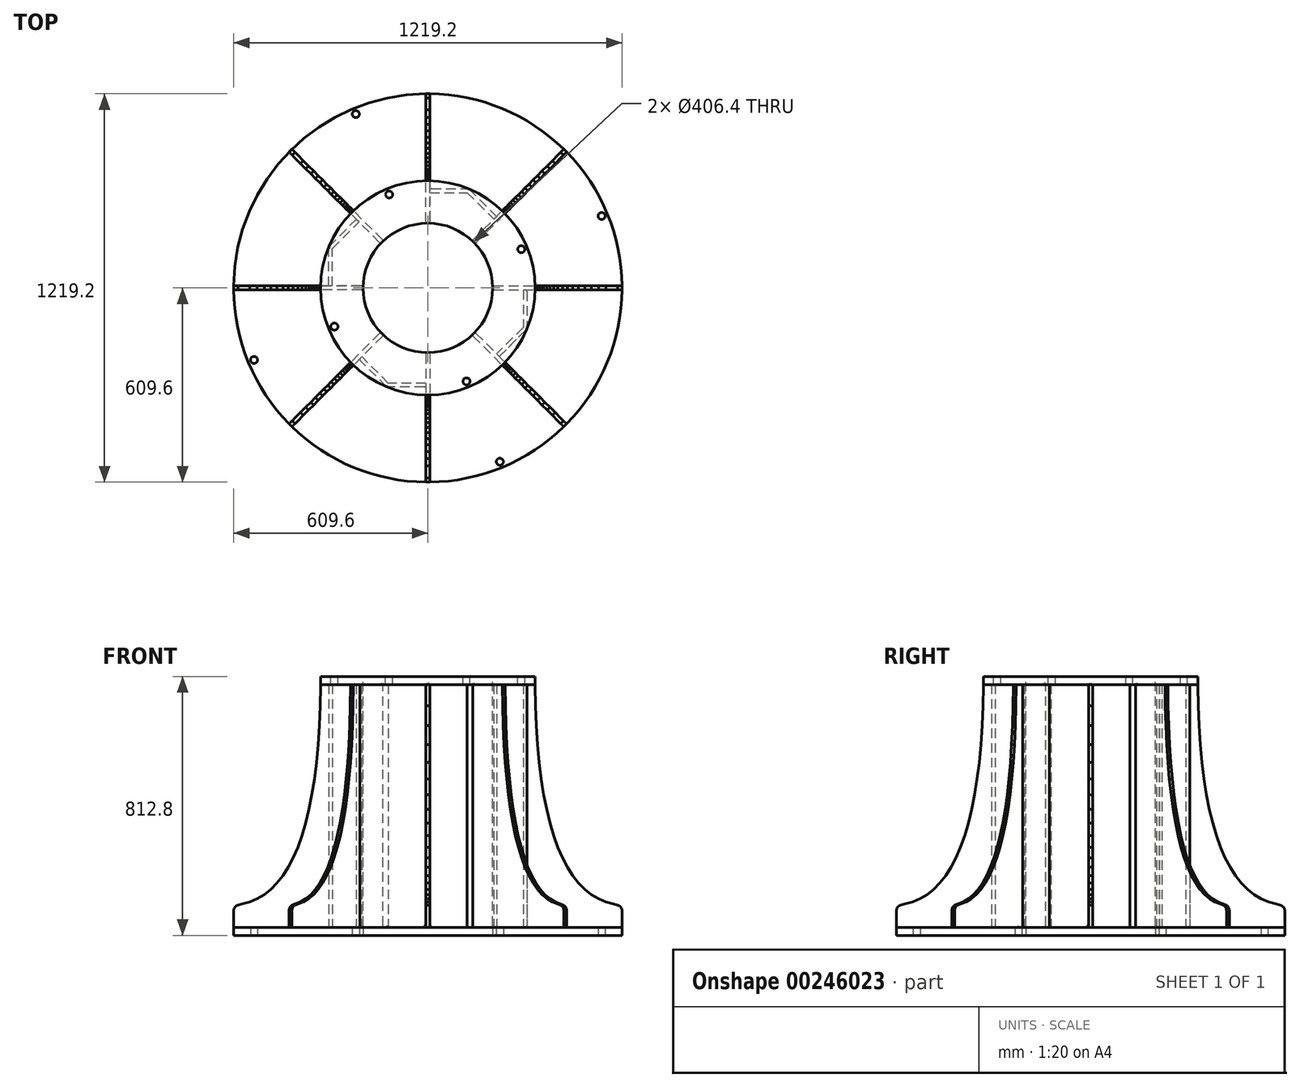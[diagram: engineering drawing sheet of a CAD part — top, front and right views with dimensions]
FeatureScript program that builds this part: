
annotation { "Feature Type Name" : "Feature", "Feature Type Description" : "" }
export const myFeature = defineFeature(function(context is Context, id is Id, definition is map)
    precondition{}
    {
        {
            var Q0;
            Q0=qCreatedBy(makeId("Top.planeOp"),FACE);
            var sketch = newSketch(context, id + "F0", { "sketchPlane" : qUnion([Q0])});
            skCircle(sketch, "E0", {"center": v(0, 0) * mm, "radius": 203.2 * mm});
            skCircle(sketch, "E1", {"center": v(0, 0) * mm, "radius": 195.26 * mm});
            skSolve(sketch);
        }
        {
            var Q0;
            Q0 = qSketchRegion(id + "F0", true);
            extrude(context, id + "F1", {"entities" : qUnion([Q0]), "depth" : 812.8 * mm});
        }
        {
            var Q0;
            Q0=makeQuery(id+"F1.opExtrude","CAP_FACE",FACE,{"disambiguationData":[OSD([sQuery(id+"F0.wireOp",EDGE,"E0"),sQuery(id+"F0.wireOp",EDGE,"E1")])],"isStart":false});
            var sketch = newSketch(context, id + "F2", { "sketchPlane" : qUnion([Q0])});
            skCircle(sketch, "E2", {"center": v(0, 0) * mm, "radius": 203.2 * mm});
            skCircle(sketch, "E3", {"center": v(0, 0) * mm, "radius": 336.55 * mm});
            skCircle(sketch, "E4", {"center": v(0, 0) * mm, "radius": 317.5 * mm, "construction": true});
            skLineSegment(sketch, "E5", {"start": v(0, 0) * mm, "end": v(500.04, 0) * mm, "construction": true});
            skLineSegment(sketch, "E6", {"start": v(0, 0) * mm, "end": v(466.48, 193.22) * mm, "construction": true});
            skCircle(sketch, "E7", {"center": v(293.33, 121.5) * mm, "radius": 11.1 * mm});
            skCircle(sketch, "E8.1.0", {"center": v(-121.5, 293.33) * mm, "radius": 11.1 * mm});
            skCircle(sketch, "E8.2.0", {"center": v(-293.33, -121.5) * mm, "radius": 11.1 * mm});
            skCircle(sketch, "E8.3.0", {"center": v(121.5, -293.33) * mm, "radius": 11.1 * mm});
            skSolve(sketch);
        }
        {
            var Q0;
            Q0 = qSketchRegion(id + "F2", true);
            extrude(context, id + "F3", {"entities" : qUnion([Q0]), "oppositeDirection" : true, "depth" : 25.4 * mm});
        }
        {
            var Q0;
            Q0=qCreatedBy(makeId("Top.planeOp"),FACE);
            var sketch = newSketch(context, id + "F4", { "sketchPlane" : qUnion([Q0])});
            skCircle(sketch, "E9", {"center": v(0, 0) * mm, "radius": 609.6 * mm});
            skCircle(sketch, "E10", {"center": v(0, 0) * mm, "radius": 203.2 * mm});
            skLineSegment(sketch, "E11", {"start": v(0, 0) * mm, "end": v(1083.18, 0) * mm, "construction": true});
            skLineSegment(sketch, "E12", {"start": v(0, 0) * mm, "end": v(912.89, 378.13) * mm, "construction": true});
            skCircle(sketch, "E13", {"center": v(0, 0) * mm, "radius": 590.55 * mm, "construction": true});
            skCircle(sketch, "E14", {"center": v(545.6, 226) * mm, "radius": 11.1 * mm});
            skCircle(sketch, "E15.1.0", {"center": v(-226, 545.6) * mm, "radius": 11.1 * mm});
            skCircle(sketch, "E15.2.0", {"center": v(-545.6, -226) * mm, "radius": 11.1 * mm});
            skCircle(sketch, "E15.3.0", {"center": v(226, -545.6) * mm, "radius": 11.1 * mm});
            skSolve(sketch);
        }
        {
            var Q0;
            Q0 = qSketchRegion(id + "F4", true);
            extrude(context, id + "F5", {"entities" : qUnion([Q0]), "depth" : 25.4 * mm});
        }
        {
            var Q0;
            Q0=qCreatedBy(makeId("Front.planeOp"),FACE);
            var sketch = newSketch(context, id + "F6", { "sketchPlane" : qUnion([Q0])});
            skLineSegment(sketch, "E16", {"start": v(0, 25.4) * mm, "end": v(726.2, 25.4) * mm, "construction": true});
            skLineSegment(sketch, "E17", {"start": v(0, 0) * mm, "end": v(737.94, 0) * mm, "construction": true});
            skLineSegment(sketch, "E18", {"start": v(0, 787.4) * mm, "end": v(419.86, 787.4) * mm, "construction": true});
            skLineSegment(sketch, "E19", {"start": v(0, 0) * mm, "end": v(0, 828.8) * mm, "construction": true});
            skLineSegment(sketch, "E20", {"start": v(0, 787.4) * mm, "end": v(336.55, 787.4) * mm});
            skLineSegment(sketch, "E21", {"start": v(336.55, 787.4) * mm, "end": v(337.85, 721.48) * mm});
            skLineSegment(sketch, "E22", {"start": v(337.85, 721.48) * mm, "end": v(340.45, 658.85) * mm});
            skLineSegment(sketch, "E23", {"start": v(340.45, 658.85) * mm, "end": v(344.35, 599.52) * mm});
            skLineSegment(sketch, "E24", {"start": v(344.35, 599.52) * mm, "end": v(349.55, 543.48) * mm});
            skLineSegment(sketch, "E25", {"start": v(349.55, 543.48) * mm, "end": v(356.05, 490.74) * mm});
            skLineSegment(sketch, "E26", {"start": v(356.05, 490.74) * mm, "end": v(363.86, 441.3) * mm});
            skLineSegment(sketch, "E27", {"start": v(363.86, 441.3) * mm, "end": v(372.96, 395.15) * mm});
            skLineSegment(sketch, "E28", {"start": v(372.96, 395.15) * mm, "end": v(383.36, 352.3) * mm});
            skLineSegment(sketch, "E29", {"start": v(383.36, 352.3) * mm, "end": v(395.06, 312.75) * mm});
            skLineSegment(sketch, "E30", {"start": v(395.06, 312.75) * mm, "end": v(408.06, 276.5) * mm});
            skLineSegment(sketch, "E31", {"start": v(408.06, 276.5) * mm, "end": v(422.37, 243.53) * mm});
            skLineSegment(sketch, "E32", {"start": v(422.37, 243.53) * mm, "end": v(437.97, 213.86) * mm});
            skLineSegment(sketch, "E33", {"start": v(437.97, 213.86) * mm, "end": v(454.87, 187.5) * mm});
            skLineSegment(sketch, "E34", {"start": v(454.87, 187.5) * mm, "end": v(473.08, 164.42) * mm});
            skLineSegment(sketch, "E35", {"start": v(473.08, 164.42) * mm, "end": v(492.58, 144.64) * mm});
            skLineSegment(sketch, "E36", {"start": v(492.58, 144.64) * mm, "end": v(513.38, 128.16) * mm});
            skLineSegment(sketch, "E37", {"start": v(513.38, 128.16) * mm, "end": v(535.49, 114.98) * mm});
            skLineSegment(sketch, "E38", {"start": v(535.49, 114.98) * mm, "end": v(558.9, 105.09) * mm});
            skLineSegment(sketch, "E39", {"start": v(558.9, 105.09) * mm, "end": v(583.6, 98.5) * mm});
            skLineSegment(sketch, "E40", {"start": v(583.6, 98.5) * mm, "end": v(595.94, 95.17) * mm});
            skArc(sketch, "E41", {"start": v(595.94, 95.17) * mm, "mid": v(605.83, 87.89) * mm, "end": v(609.6, 76.2) * mm});
            skLineSegment(sketch, "E42", {"start": v(609.6, 76.2) * mm, "end": v(609.6, 25.4) * mm});
            skLineSegment(sketch, "E43", {"start": v(609.6, 25.4) * mm, "end": v(0, 25.4) * mm});
            skLineSegment(sketch, "E44", {"start": v(0, 25.4) * mm, "end": v(0, 787.4) * mm});
            skSolve(sketch);
        }
        {
            var Q0;
            Q0 = qSketchRegion(id + "F6", true);
            extrude(context, id + "F7", {"entities" : qUnion([Q0]), "depth" : 12.7 * mm, "symmetric" : true});
        }
        {
            var Q0;
            Q0=qCreatedBy(makeId("Top.planeOp"),FACE);
            var sketch = newSketch(context, id + "F8", { "sketchPlane" : qUnion([Q0])});
            skCircle(sketch, "E45", {"center": v(0, 0) * mm, "radius": 203.2 * mm});
            skSolve(sketch);
        }
        {
            var Q0;
            Q0=makeQuery(id+"F8.imprint","IMPRINT",FACE,{"disambiguationData":[TD([[makeQuery(id+"F8.imprint","IMPRINT",EDGE,{"derivedFrom":sQuery(id+"F8.wireOp",EDGE,"E45")}),1.0]])]});
            extrude(context, id + "F9", {"entities" : qUnion([Q0]), "operationType" : NewBodyOperationType.REMOVE, "depth" : 812.8 * mm, "offsetDistance" : 25 * mm});
        }
        {
            var Q0;
            Q0=makeQuery(id+"F7.opExtrude","SWEPT_BODY",BODY,{"disambiguationData":[OSD([sQuery(id+"F6.wireOp",EDGE,"E20"),sQuery(id+"F6.wireOp",EDGE,"E21"),sQuery(id+"F6.wireOp",EDGE,"E22"),sQuery(id+"F6.wireOp",EDGE,"E23"),sQuery(id+"F6.wireOp",EDGE,"E24"),sQuery(id+"F6.wireOp",EDGE,"E25"),sQuery(id+"F6.wireOp",EDGE,"E26"),sQuery(id+"F6.wireOp",EDGE,"E27"),sQuery(id+"F6.wireOp",EDGE,"E28"),sQuery(id+"F6.wireOp",EDGE,"E29"),sQuery(id+"F6.wireOp",EDGE,"E30"),sQuery(id+"F6.wireOp",EDGE,"E31"),sQuery(id+"F6.wireOp",EDGE,"E32"),sQuery(id+"F6.wireOp",EDGE,"E33"),sQuery(id+"F6.wireOp",EDGE,"E34"),sQuery(id+"F6.wireOp",EDGE,"E35"),sQuery(id+"F6.wireOp",EDGE,"E36"),sQuery(id+"F6.wireOp",EDGE,"E37"),sQuery(id+"F6.wireOp",EDGE,"E38"),sQuery(id+"F6.wireOp",EDGE,"E39"),sQuery(id+"F6.wireOp",EDGE,"E40"),sQuery(id+"F6.wireOp",EDGE,"E41"),sQuery(id+"F6.wireOp",EDGE,"E42"),sQuery(id+"F6.wireOp",EDGE,"E43"),sQuery(id+"F6.wireOp",EDGE,"E44")])]});
            var Q1;
            Q1=sQuery(id+"F6.wireOp",EDGE,"E19");
            circularPattern(context, id + "F10", {"entities" : qUnion([Q0]), "axis" : qUnion([Q1]), "angle" : 360 * degree, "instanceCount" : 8, "equalSpace" : true});
        }
        {
            var Q0;
            Q0=makeQuery(id+"F5.opExtrude","CAP_FACE",FACE,{"disambiguationData":[OSD([sQuery(id+"F4.wireOp",EDGE,"E9"),sQuery(id+"F4.wireOp",EDGE,"E10"),sQuery(id+"F4.wireOp",EDGE,"E14"),sQuery(id+"F4.wireOp",EDGE,"E15.1.0"),sQuery(id+"F4.wireOp",EDGE,"E15.2.0"),sQuery(id+"F4.wireOp",EDGE,"E15.3.0")])],"isStart":false});
            var sketch = newSketch(context, id + "F11", { "sketchPlane" : qUnion([Q0])});
            skCircle(sketch, "E46", {"center": v(0, 0) * mm, "radius": 323.85 * mm, "construction": true});
            skCircle(sketch, "E47", {"center": v(0, 0) * mm, "radius": 336.55 * mm, "construction": true});
            skLineSegment(sketch, "E48", {"start": v(0, 0) * mm, "end": v(904.77, 0) * mm, "construction": true});
            skLineSegment(sketch, "E49", {"start": v(0, 0) * mm, "end": v(0, 713.88) * mm, "construction": true});
            skLineSegment(sketch, "E50", {"start": v(0, 0) * mm, "end": v(749.37, 310.4) * mm, "construction": true});
            skLineSegment(sketch, "E51.7", {"start": v(128.8, 310.93) * mm, "end": v(215.37, 224.35) * mm});
            skLineSegment(sketch, "E52.7", {"start": v(123.93, 299.2) * mm, "end": v(207.08, 216.06) * mm});
            skLineSegment(sketch, "E53.1.1", {"start": v(0, 0) * mm, "end": v(504.79, 504.79) * mm, "construction": true});
            skLineSegment(sketch, "E54.trimOffspring", {"start": v(207.08, 216.06) * mm, "end": v(215.37, 224.35) * mm});
            skLineSegment(sketch, "E55.trimOffspring", {"start": v(6.35, 299.2) * mm, "end": v(123.93, 299.2) * mm});
            skLineSegment(sketch, "E56.trimOffspring", {"start": v(6.35, 310.93) * mm, "end": v(128.8, 310.93) * mm});
            skLineSegment(sketch, "E57.trimOffspring", {"start": v(6.35, 299.2) * mm, "end": v(6.35, 310.93) * mm});
            skSolve(sketch);
        }
        {
            var Q0;
            Q0=makeQuery(id+"F11.imprint","IMPRINT",FACE,{"disambiguationData":[TD([[makeQuery(id+"F11.imprint","IMPRINT",EDGE,{"derivedFrom":sQuery(id+"F11.wireOp",EDGE,"E51.7")}),-1.0]])]});
            extrude(context, id + "F12", {"entities" : qUnion([Q0]), "depth" : 762 * mm});
        }
        {
            var Q0;
            Q0=makeQuery(id+"F12.opExtrude","SWEPT_BODY",BODY,{"disambiguationData":[OSD([sQuery(id+"F11.wireOp",EDGE,"E51.7"),sQuery(id+"F11.wireOp",EDGE,"E52.7"),sQuery(id+"F11.wireOp",EDGE,"E54.trimOffspring"),sQuery(id+"F11.wireOp",EDGE,"E55.trimOffspring"),sQuery(id+"F11.wireOp",EDGE,"E56.trimOffspring"),sQuery(id+"F11.wireOp",EDGE,"E57.trimOffspring")])]});
            var Q1;
            Q1=sQuery(id+"F6.wireOp",EDGE,"E44");
            circularPattern(context, id + "F13", {"entities" : qUnion([Q0]), "axis" : qUnion([Q1]), "angle" : 360 * degree, "instanceCount" : 4, "equalSpace" : true});
        }
        {
            var Q0;
            Q0=makeQuery(id+"F3.opExtrude","SWEPT_BODY",BODY,{"disambiguationData":[OSD([sQuery(id+"F2.wireOp",EDGE,"E2"),sQuery(id+"F2.wireOp",EDGE,"E3"),sQuery(id+"F2.wireOp",EDGE,"E7"),sQuery(id+"F2.wireOp",EDGE,"E8.1.0"),sQuery(id+"F2.wireOp",EDGE,"E8.2.0"),sQuery(id+"F2.wireOp",EDGE,"E8.3.0")])]});
            var Q1;
            Q1=makeQuery(id+"F10.opPattern","COPY",BODY,{"derivedFrom":makeQuery(id+"F7.opExtrude","SWEPT_BODY",BODY,{"disambiguationData":[OSD([sQuery(id+"F6.wireOp",EDGE,"E20"),sQuery(id+"F6.wireOp",EDGE,"E21"),sQuery(id+"F6.wireOp",EDGE,"E22"),sQuery(id+"F6.wireOp",EDGE,"E23"),sQuery(id+"F6.wireOp",EDGE,"E24"),sQuery(id+"F6.wireOp",EDGE,"E25"),sQuery(id+"F6.wireOp",EDGE,"E26"),sQuery(id+"F6.wireOp",EDGE,"E27"),sQuery(id+"F6.wireOp",EDGE,"E28"),sQuery(id+"F6.wireOp",EDGE,"E29"),sQuery(id+"F6.wireOp",EDGE,"E30"),sQuery(id+"F6.wireOp",EDGE,"E31"),sQuery(id+"F6.wireOp",EDGE,"E32"),sQuery(id+"F6.wireOp",EDGE,"E33"),sQuery(id+"F6.wireOp",EDGE,"E34"),sQuery(id+"F6.wireOp",EDGE,"E35"),sQuery(id+"F6.wireOp",EDGE,"E36"),sQuery(id+"F6.wireOp",EDGE,"E37"),sQuery(id+"F6.wireOp",EDGE,"E38"),sQuery(id+"F6.wireOp",EDGE,"E39"),sQuery(id+"F6.wireOp",EDGE,"E40"),sQuery(id+"F6.wireOp",EDGE,"E41"),sQuery(id+"F6.wireOp",EDGE,"E42"),sQuery(id+"F6.wireOp",EDGE,"E43"),sQuery(id+"F6.wireOp",EDGE,"E44")])]}),"instanceName":"7"});
            var Q2;
            Q2=makeQuery(id+"F7.opExtrude","SWEPT_BODY",BODY,{"disambiguationData":[OSD([sQuery(id+"F6.wireOp",EDGE,"E20"),sQuery(id+"F6.wireOp",EDGE,"E21"),sQuery(id+"F6.wireOp",EDGE,"E22"),sQuery(id+"F6.wireOp",EDGE,"E23"),sQuery(id+"F6.wireOp",EDGE,"E24"),sQuery(id+"F6.wireOp",EDGE,"E25"),sQuery(id+"F6.wireOp",EDGE,"E26"),sQuery(id+"F6.wireOp",EDGE,"E27"),sQuery(id+"F6.wireOp",EDGE,"E28"),sQuery(id+"F6.wireOp",EDGE,"E29"),sQuery(id+"F6.wireOp",EDGE,"E30"),sQuery(id+"F6.wireOp",EDGE,"E31"),sQuery(id+"F6.wireOp",EDGE,"E32"),sQuery(id+"F6.wireOp",EDGE,"E33"),sQuery(id+"F6.wireOp",EDGE,"E34"),sQuery(id+"F6.wireOp",EDGE,"E35"),sQuery(id+"F6.wireOp",EDGE,"E36"),sQuery(id+"F6.wireOp",EDGE,"E37"),sQuery(id+"F6.wireOp",EDGE,"E38"),sQuery(id+"F6.wireOp",EDGE,"E39"),sQuery(id+"F6.wireOp",EDGE,"E40"),sQuery(id+"F6.wireOp",EDGE,"E41"),sQuery(id+"F6.wireOp",EDGE,"E42"),sQuery(id+"F6.wireOp",EDGE,"E43"),sQuery(id+"F6.wireOp",EDGE,"E44")])]});
            var Q3;
            Q3=makeQuery(id+"F10.opPattern","COPY",BODY,{"derivedFrom":makeQuery(id+"F7.opExtrude","SWEPT_BODY",BODY,{"disambiguationData":[OSD([sQuery(id+"F6.wireOp",EDGE,"E20"),sQuery(id+"F6.wireOp",EDGE,"E21"),sQuery(id+"F6.wireOp",EDGE,"E22"),sQuery(id+"F6.wireOp",EDGE,"E23"),sQuery(id+"F6.wireOp",EDGE,"E24"),sQuery(id+"F6.wireOp",EDGE,"E25"),sQuery(id+"F6.wireOp",EDGE,"E26"),sQuery(id+"F6.wireOp",EDGE,"E27"),sQuery(id+"F6.wireOp",EDGE,"E28"),sQuery(id+"F6.wireOp",EDGE,"E29"),sQuery(id+"F6.wireOp",EDGE,"E30"),sQuery(id+"F6.wireOp",EDGE,"E31"),sQuery(id+"F6.wireOp",EDGE,"E32"),sQuery(id+"F6.wireOp",EDGE,"E33"),sQuery(id+"F6.wireOp",EDGE,"E34"),sQuery(id+"F6.wireOp",EDGE,"E35"),sQuery(id+"F6.wireOp",EDGE,"E36"),sQuery(id+"F6.wireOp",EDGE,"E37"),sQuery(id+"F6.wireOp",EDGE,"E38"),sQuery(id+"F6.wireOp",EDGE,"E39"),sQuery(id+"F6.wireOp",EDGE,"E40"),sQuery(id+"F6.wireOp",EDGE,"E41"),sQuery(id+"F6.wireOp",EDGE,"E42"),sQuery(id+"F6.wireOp",EDGE,"E43"),sQuery(id+"F6.wireOp",EDGE,"E44")])]}),"instanceName":"1"});
            var Q4;
            Q4=makeQuery(id+"F10.opPattern","COPY",BODY,{"derivedFrom":makeQuery(id+"F7.opExtrude","SWEPT_BODY",BODY,{"disambiguationData":[OSD([sQuery(id+"F6.wireOp",EDGE,"E20"),sQuery(id+"F6.wireOp",EDGE,"E21"),sQuery(id+"F6.wireOp",EDGE,"E22"),sQuery(id+"F6.wireOp",EDGE,"E23"),sQuery(id+"F6.wireOp",EDGE,"E24"),sQuery(id+"F6.wireOp",EDGE,"E25"),sQuery(id+"F6.wireOp",EDGE,"E26"),sQuery(id+"F6.wireOp",EDGE,"E27"),sQuery(id+"F6.wireOp",EDGE,"E28"),sQuery(id+"F6.wireOp",EDGE,"E29"),sQuery(id+"F6.wireOp",EDGE,"E30"),sQuery(id+"F6.wireOp",EDGE,"E31"),sQuery(id+"F6.wireOp",EDGE,"E32"),sQuery(id+"F6.wireOp",EDGE,"E33"),sQuery(id+"F6.wireOp",EDGE,"E34"),sQuery(id+"F6.wireOp",EDGE,"E35"),sQuery(id+"F6.wireOp",EDGE,"E36"),sQuery(id+"F6.wireOp",EDGE,"E37"),sQuery(id+"F6.wireOp",EDGE,"E38"),sQuery(id+"F6.wireOp",EDGE,"E39"),sQuery(id+"F6.wireOp",EDGE,"E40"),sQuery(id+"F6.wireOp",EDGE,"E41"),sQuery(id+"F6.wireOp",EDGE,"E42"),sQuery(id+"F6.wireOp",EDGE,"E43"),sQuery(id+"F6.wireOp",EDGE,"E44")])]}),"instanceName":"2"});
            var Q5;
            Q5=makeQuery(id+"F10.opPattern","COPY",BODY,{"derivedFrom":makeQuery(id+"F7.opExtrude","SWEPT_BODY",BODY,{"disambiguationData":[OSD([sQuery(id+"F6.wireOp",EDGE,"E20"),sQuery(id+"F6.wireOp",EDGE,"E21"),sQuery(id+"F6.wireOp",EDGE,"E22"),sQuery(id+"F6.wireOp",EDGE,"E23"),sQuery(id+"F6.wireOp",EDGE,"E24"),sQuery(id+"F6.wireOp",EDGE,"E25"),sQuery(id+"F6.wireOp",EDGE,"E26"),sQuery(id+"F6.wireOp",EDGE,"E27"),sQuery(id+"F6.wireOp",EDGE,"E28"),sQuery(id+"F6.wireOp",EDGE,"E29"),sQuery(id+"F6.wireOp",EDGE,"E30"),sQuery(id+"F6.wireOp",EDGE,"E31"),sQuery(id+"F6.wireOp",EDGE,"E32"),sQuery(id+"F6.wireOp",EDGE,"E33"),sQuery(id+"F6.wireOp",EDGE,"E34"),sQuery(id+"F6.wireOp",EDGE,"E35"),sQuery(id+"F6.wireOp",EDGE,"E36"),sQuery(id+"F6.wireOp",EDGE,"E37"),sQuery(id+"F6.wireOp",EDGE,"E38"),sQuery(id+"F6.wireOp",EDGE,"E39"),sQuery(id+"F6.wireOp",EDGE,"E40"),sQuery(id+"F6.wireOp",EDGE,"E41"),sQuery(id+"F6.wireOp",EDGE,"E42"),sQuery(id+"F6.wireOp",EDGE,"E43"),sQuery(id+"F6.wireOp",EDGE,"E44")])]}),"instanceName":"3"});
            var Q6;
            Q6=makeQuery(id+"F10.opPattern","COPY",BODY,{"derivedFrom":makeQuery(id+"F7.opExtrude","SWEPT_BODY",BODY,{"disambiguationData":[OSD([sQuery(id+"F6.wireOp",EDGE,"E20"),sQuery(id+"F6.wireOp",EDGE,"E21"),sQuery(id+"F6.wireOp",EDGE,"E22"),sQuery(id+"F6.wireOp",EDGE,"E23"),sQuery(id+"F6.wireOp",EDGE,"E24"),sQuery(id+"F6.wireOp",EDGE,"E25"),sQuery(id+"F6.wireOp",EDGE,"E26"),sQuery(id+"F6.wireOp",EDGE,"E27"),sQuery(id+"F6.wireOp",EDGE,"E28"),sQuery(id+"F6.wireOp",EDGE,"E29"),sQuery(id+"F6.wireOp",EDGE,"E30"),sQuery(id+"F6.wireOp",EDGE,"E31"),sQuery(id+"F6.wireOp",EDGE,"E32"),sQuery(id+"F6.wireOp",EDGE,"E33"),sQuery(id+"F6.wireOp",EDGE,"E34"),sQuery(id+"F6.wireOp",EDGE,"E35"),sQuery(id+"F6.wireOp",EDGE,"E36"),sQuery(id+"F6.wireOp",EDGE,"E37"),sQuery(id+"F6.wireOp",EDGE,"E38"),sQuery(id+"F6.wireOp",EDGE,"E39"),sQuery(id+"F6.wireOp",EDGE,"E40"),sQuery(id+"F6.wireOp",EDGE,"E41"),sQuery(id+"F6.wireOp",EDGE,"E42"),sQuery(id+"F6.wireOp",EDGE,"E43"),sQuery(id+"F6.wireOp",EDGE,"E44")])]}),"instanceName":"4"});
            var Q7;
            Q7=makeQuery(id+"F10.opPattern","COPY",BODY,{"derivedFrom":makeQuery(id+"F7.opExtrude","SWEPT_BODY",BODY,{"disambiguationData":[OSD([sQuery(id+"F6.wireOp",EDGE,"E20"),sQuery(id+"F6.wireOp",EDGE,"E21"),sQuery(id+"F6.wireOp",EDGE,"E22"),sQuery(id+"F6.wireOp",EDGE,"E23"),sQuery(id+"F6.wireOp",EDGE,"E24"),sQuery(id+"F6.wireOp",EDGE,"E25"),sQuery(id+"F6.wireOp",EDGE,"E26"),sQuery(id+"F6.wireOp",EDGE,"E27"),sQuery(id+"F6.wireOp",EDGE,"E28"),sQuery(id+"F6.wireOp",EDGE,"E29"),sQuery(id+"F6.wireOp",EDGE,"E30"),sQuery(id+"F6.wireOp",EDGE,"E31"),sQuery(id+"F6.wireOp",EDGE,"E32"),sQuery(id+"F6.wireOp",EDGE,"E33"),sQuery(id+"F6.wireOp",EDGE,"E34"),sQuery(id+"F6.wireOp",EDGE,"E35"),sQuery(id+"F6.wireOp",EDGE,"E36"),sQuery(id+"F6.wireOp",EDGE,"E37"),sQuery(id+"F6.wireOp",EDGE,"E38"),sQuery(id+"F6.wireOp",EDGE,"E39"),sQuery(id+"F6.wireOp",EDGE,"E40"),sQuery(id+"F6.wireOp",EDGE,"E41"),sQuery(id+"F6.wireOp",EDGE,"E42"),sQuery(id+"F6.wireOp",EDGE,"E43"),sQuery(id+"F6.wireOp",EDGE,"E44")])]}),"instanceName":"5"});
            var Q8;
            Q8=makeQuery(id+"F10.opPattern","COPY",BODY,{"derivedFrom":makeQuery(id+"F7.opExtrude","SWEPT_BODY",BODY,{"disambiguationData":[OSD([sQuery(id+"F6.wireOp",EDGE,"E20"),sQuery(id+"F6.wireOp",EDGE,"E21"),sQuery(id+"F6.wireOp",EDGE,"E22"),sQuery(id+"F6.wireOp",EDGE,"E23"),sQuery(id+"F6.wireOp",EDGE,"E24"),sQuery(id+"F6.wireOp",EDGE,"E25"),sQuery(id+"F6.wireOp",EDGE,"E26"),sQuery(id+"F6.wireOp",EDGE,"E27"),sQuery(id+"F6.wireOp",EDGE,"E28"),sQuery(id+"F6.wireOp",EDGE,"E29"),sQuery(id+"F6.wireOp",EDGE,"E30"),sQuery(id+"F6.wireOp",EDGE,"E31"),sQuery(id+"F6.wireOp",EDGE,"E32"),sQuery(id+"F6.wireOp",EDGE,"E33"),sQuery(id+"F6.wireOp",EDGE,"E34"),sQuery(id+"F6.wireOp",EDGE,"E35"),sQuery(id+"F6.wireOp",EDGE,"E36"),sQuery(id+"F6.wireOp",EDGE,"E37"),sQuery(id+"F6.wireOp",EDGE,"E38"),sQuery(id+"F6.wireOp",EDGE,"E39"),sQuery(id+"F6.wireOp",EDGE,"E40"),sQuery(id+"F6.wireOp",EDGE,"E41"),sQuery(id+"F6.wireOp",EDGE,"E42"),sQuery(id+"F6.wireOp",EDGE,"E43"),sQuery(id+"F6.wireOp",EDGE,"E44")])]}),"instanceName":"6"});
            booleanBodies(context, id + "F14", {"operationType" : BooleanOperationType.UNION, "tools" : qUnion([Q0, Q1, Q2, Q3, Q4, Q5, Q6, Q7, Q8])});
        }
        {
            var Q0;
            {var subQ0=sQuery(id+"F6.wireOp",EDGE,"E43");Q0=makeQuery(id+"F14.opBoolean","SPLIT",EDGE,{"disambiguationData":[TD([makeQuery(id+"F1.opExtrude","SWEPT_FACE",FACE,{"disambiguationData":[OSD([sQuery(id+"F0.wireOp",EDGE,"E0")])]})])],"derivedFrom":makeQuery(id+"F10.opPattern","COPY",EDGE,{"derivedFrom":makeQuery(id+"F7.opExtrude","CAP_EDGE",EDGE,{"disambiguationData":[OSD([subQ0])],"isStart":false}),"instanceName":"3"})});}
            var Q1;
            {var subQ0=sQuery(id+"F4.wireOp",EDGE,"E10");var subQ1=sQuery(id+"F6.wireOp",EDGE,"E44");var subQ2=sQuery(id+"F6.wireOp",EDGE,"E43");var subQ3=sQuery(id+"F6.wireOp",EDGE,"E42");var subQ4=sQuery(id+"F6.wireOp",EDGE,"E41");var subQ5=sQuery(id+"F6.wireOp",EDGE,"E40");var subQ6=sQuery(id+"F6.wireOp",EDGE,"E39");var subQ7=sQuery(id+"F6.wireOp",EDGE,"E38");var subQ8=sQuery(id+"F6.wireOp",EDGE,"E37");var subQ9=sQuery(id+"F6.wireOp",EDGE,"E36");var subQ10=sQuery(id+"F6.wireOp",EDGE,"E35");var subQ11=sQuery(id+"F6.wireOp",EDGE,"E34");var subQ12=sQuery(id+"F6.wireOp",EDGE,"E33");var subQ13=sQuery(id+"F6.wireOp",EDGE,"E32");var subQ14=sQuery(id+"F6.wireOp",EDGE,"E31");var subQ15=sQuery(id+"F6.wireOp",EDGE,"E30");var subQ16=sQuery(id+"F6.wireOp",EDGE,"E29");var subQ17=sQuery(id+"F6.wireOp",EDGE,"E28");var subQ18=sQuery(id+"F6.wireOp",EDGE,"E27");var subQ19=sQuery(id+"F6.wireOp",EDGE,"E26");var subQ20=sQuery(id+"F6.wireOp",EDGE,"E25");var subQ21=sQuery(id+"F6.wireOp",EDGE,"E24");var subQ22=sQuery(id+"F6.wireOp",EDGE,"E23");var subQ23=sQuery(id+"F6.wireOp",EDGE,"E22");var subQ24=sQuery(id+"F6.wireOp",EDGE,"E21");var subQ25=sQuery(id+"F6.wireOp",EDGE,"E20");Q1=makeQuery(id+"F14.opBoolean","SPLIT",EDGE,{"disambiguationData":[TD([makeQuery(id+"F10.opPattern","COPY",FACE,{"derivedFrom":makeQuery(id+"F7.opExtrude","CAP_FACE",FACE,{"disambiguationData":[OSD([subQ25,subQ24,subQ23,subQ22,subQ21,subQ20,subQ19,subQ18,subQ17,subQ16,subQ15,subQ14,subQ13,subQ12,subQ11,subQ10,subQ9,subQ8,subQ7,subQ6,subQ5,subQ4,subQ3,subQ2,subQ1])],"isStart":true}),"instanceName":"2"})])],"derivedFrom":makeQuery(id+"F5.opExtrude","CAP_EDGE",EDGE,{"disambiguationData":[OSD([subQ0])],"isStart":false})});}
            var Q2;
            {var subQ0=sQuery(id+"F6.wireOp",EDGE,"E43");Q2=makeQuery(id+"F14.opBoolean","SPLIT",EDGE,{"disambiguationData":[TD([makeQuery(id+"F1.opExtrude","SWEPT_FACE",FACE,{"disambiguationData":[OSD([sQuery(id+"F0.wireOp",EDGE,"E0")])]})])],"derivedFrom":makeQuery(id+"F10.opPattern","COPY",EDGE,{"derivedFrom":makeQuery(id+"F7.opExtrude","CAP_EDGE",EDGE,{"disambiguationData":[OSD([subQ0])],"isStart":true}),"instanceName":"2"})});}
            var Q3;
            {var subQ0=sQuery(id+"F6.wireOp",EDGE,"E43");Q3=makeQuery(id+"F14.opBoolean","SPLIT",EDGE,{"disambiguationData":[TD([makeQuery(id+"F1.opExtrude","SWEPT_FACE",FACE,{"disambiguationData":[OSD([sQuery(id+"F0.wireOp",EDGE,"E0")])]})])],"derivedFrom":makeQuery(id+"F10.opPattern","COPY",EDGE,{"derivedFrom":makeQuery(id+"F7.opExtrude","CAP_EDGE",EDGE,{"disambiguationData":[OSD([subQ0])],"isStart":false}),"instanceName":"2"})});}
            var Q4;
            {var subQ0=sQuery(id+"F4.wireOp",EDGE,"E10");var subQ1=sQuery(id+"F6.wireOp",EDGE,"E44");var subQ2=sQuery(id+"F6.wireOp",EDGE,"E43");var subQ3=sQuery(id+"F6.wireOp",EDGE,"E42");var subQ4=sQuery(id+"F6.wireOp",EDGE,"E41");var subQ5=sQuery(id+"F6.wireOp",EDGE,"E40");var subQ6=sQuery(id+"F6.wireOp",EDGE,"E39");var subQ7=sQuery(id+"F6.wireOp",EDGE,"E38");var subQ8=sQuery(id+"F6.wireOp",EDGE,"E37");var subQ9=sQuery(id+"F6.wireOp",EDGE,"E36");var subQ10=sQuery(id+"F6.wireOp",EDGE,"E35");var subQ11=sQuery(id+"F6.wireOp",EDGE,"E34");var subQ12=sQuery(id+"F6.wireOp",EDGE,"E33");var subQ13=sQuery(id+"F6.wireOp",EDGE,"E32");var subQ14=sQuery(id+"F6.wireOp",EDGE,"E31");var subQ15=sQuery(id+"F6.wireOp",EDGE,"E30");var subQ16=sQuery(id+"F6.wireOp",EDGE,"E29");var subQ17=sQuery(id+"F6.wireOp",EDGE,"E28");var subQ18=sQuery(id+"F6.wireOp",EDGE,"E27");var subQ19=sQuery(id+"F6.wireOp",EDGE,"E26");var subQ20=sQuery(id+"F6.wireOp",EDGE,"E25");var subQ21=sQuery(id+"F6.wireOp",EDGE,"E24");var subQ22=sQuery(id+"F6.wireOp",EDGE,"E23");var subQ23=sQuery(id+"F6.wireOp",EDGE,"E22");var subQ24=sQuery(id+"F6.wireOp",EDGE,"E21");var subQ25=sQuery(id+"F6.wireOp",EDGE,"E20");Q4=makeQuery(id+"F14.opBoolean","SPLIT",EDGE,{"disambiguationData":[TD([makeQuery(id+"F10.opPattern","COPY",FACE,{"derivedFrom":makeQuery(id+"F7.opExtrude","CAP_FACE",FACE,{"disambiguationData":[OSD([subQ25,subQ24,subQ23,subQ22,subQ21,subQ20,subQ19,subQ18,subQ17,subQ16,subQ15,subQ14,subQ13,subQ12,subQ11,subQ10,subQ9,subQ8,subQ7,subQ6,subQ5,subQ4,subQ3,subQ2,subQ1])],"isStart":true}),"instanceName":"1"})])],"derivedFrom":makeQuery(id+"F5.opExtrude","CAP_EDGE",EDGE,{"disambiguationData":[OSD([subQ0])],"isStart":false})});}
            var Q5;
            {var subQ0=sQuery(id+"F6.wireOp",EDGE,"E43");Q5=makeQuery(id+"F14.opBoolean","SPLIT",EDGE,{"disambiguationData":[TD([makeQuery(id+"F1.opExtrude","SWEPT_FACE",FACE,{"disambiguationData":[OSD([sQuery(id+"F0.wireOp",EDGE,"E0")])]})])],"derivedFrom":makeQuery(id+"F10.opPattern","COPY",EDGE,{"derivedFrom":makeQuery(id+"F7.opExtrude","CAP_EDGE",EDGE,{"disambiguationData":[OSD([subQ0])],"isStart":true}),"instanceName":"1"})});}
            var Q6;
            {var subQ0=sQuery(id+"F6.wireOp",EDGE,"E43");Q6=makeQuery(id+"F14.opBoolean","SPLIT",EDGE,{"disambiguationData":[TD([makeQuery(id+"F1.opExtrude","SWEPT_FACE",FACE,{"disambiguationData":[OSD([sQuery(id+"F0.wireOp",EDGE,"E0")])]})])],"derivedFrom":makeQuery(id+"F10.opPattern","COPY",EDGE,{"derivedFrom":makeQuery(id+"F7.opExtrude","CAP_EDGE",EDGE,{"disambiguationData":[OSD([subQ0])],"isStart":false}),"instanceName":"1"})});}
            var Q7;
            {var subQ0=sQuery(id+"F4.wireOp",EDGE,"E10");var subQ1=sQuery(id+"F6.wireOp",EDGE,"E44");var subQ2=sQuery(id+"F6.wireOp",EDGE,"E43");var subQ3=sQuery(id+"F6.wireOp",EDGE,"E42");var subQ4=sQuery(id+"F6.wireOp",EDGE,"E41");var subQ5=sQuery(id+"F6.wireOp",EDGE,"E40");var subQ6=sQuery(id+"F6.wireOp",EDGE,"E39");var subQ7=sQuery(id+"F6.wireOp",EDGE,"E38");var subQ8=sQuery(id+"F6.wireOp",EDGE,"E37");var subQ9=sQuery(id+"F6.wireOp",EDGE,"E36");var subQ10=sQuery(id+"F6.wireOp",EDGE,"E35");var subQ11=sQuery(id+"F6.wireOp",EDGE,"E34");var subQ12=sQuery(id+"F6.wireOp",EDGE,"E33");var subQ13=sQuery(id+"F6.wireOp",EDGE,"E32");var subQ14=sQuery(id+"F6.wireOp",EDGE,"E31");var subQ15=sQuery(id+"F6.wireOp",EDGE,"E30");var subQ16=sQuery(id+"F6.wireOp",EDGE,"E29");var subQ17=sQuery(id+"F6.wireOp",EDGE,"E28");var subQ18=sQuery(id+"F6.wireOp",EDGE,"E27");var subQ19=sQuery(id+"F6.wireOp",EDGE,"E26");var subQ20=sQuery(id+"F6.wireOp",EDGE,"E25");var subQ21=sQuery(id+"F6.wireOp",EDGE,"E24");var subQ22=sQuery(id+"F6.wireOp",EDGE,"E23");var subQ23=sQuery(id+"F6.wireOp",EDGE,"E22");var subQ24=sQuery(id+"F6.wireOp",EDGE,"E21");var subQ25=sQuery(id+"F6.wireOp",EDGE,"E20");Q7=makeQuery(id+"F14.opBoolean","SPLIT",EDGE,{"disambiguationData":[TD([makeQuery(id+"F7.opExtrude","CAP_FACE",FACE,{"disambiguationData":[OSD([subQ25,subQ24,subQ23,subQ22,subQ21,subQ20,subQ19,subQ18,subQ17,subQ16,subQ15,subQ14,subQ13,subQ12,subQ11,subQ10,subQ9,subQ8,subQ7,subQ6,subQ5,subQ4,subQ3,subQ2,subQ1])],"isStart":true})])],"derivedFrom":makeQuery(id+"F5.opExtrude","CAP_EDGE",EDGE,{"disambiguationData":[OSD([subQ0])],"isStart":false})});}
            var Q8;
            {var subQ0=sQuery(id+"F6.wireOp",EDGE,"E43");Q8=makeQuery(id+"F14.opBoolean","SPLIT",EDGE,{"disambiguationData":[TD([makeQuery(id+"F1.opExtrude","SWEPT_FACE",FACE,{"disambiguationData":[OSD([sQuery(id+"F0.wireOp",EDGE,"E0")])]})])],"derivedFrom":makeQuery(id+"F7.opExtrude","CAP_EDGE",EDGE,{"disambiguationData":[OSD([subQ0])],"isStart":true})});}
            var Q9;
            {var subQ0=sQuery(id+"F6.wireOp",EDGE,"E43");Q9=makeQuery(id+"F14.opBoolean","SPLIT",EDGE,{"disambiguationData":[TD([makeQuery(id+"F1.opExtrude","SWEPT_FACE",FACE,{"disambiguationData":[OSD([sQuery(id+"F0.wireOp",EDGE,"E0")])]})])],"derivedFrom":makeQuery(id+"F7.opExtrude","CAP_EDGE",EDGE,{"disambiguationData":[OSD([subQ0])],"isStart":false})});}
            var Q10;
            {var subQ0=sQuery(id+"F4.wireOp",EDGE,"E10");var subQ1=sQuery(id+"F6.wireOp",EDGE,"E44");var subQ2=sQuery(id+"F6.wireOp",EDGE,"E43");var subQ3=sQuery(id+"F6.wireOp",EDGE,"E42");var subQ4=sQuery(id+"F6.wireOp",EDGE,"E41");var subQ5=sQuery(id+"F6.wireOp",EDGE,"E40");var subQ6=sQuery(id+"F6.wireOp",EDGE,"E39");var subQ7=sQuery(id+"F6.wireOp",EDGE,"E38");var subQ8=sQuery(id+"F6.wireOp",EDGE,"E37");var subQ9=sQuery(id+"F6.wireOp",EDGE,"E36");var subQ10=sQuery(id+"F6.wireOp",EDGE,"E35");var subQ11=sQuery(id+"F6.wireOp",EDGE,"E34");var subQ12=sQuery(id+"F6.wireOp",EDGE,"E33");var subQ13=sQuery(id+"F6.wireOp",EDGE,"E32");var subQ14=sQuery(id+"F6.wireOp",EDGE,"E31");var subQ15=sQuery(id+"F6.wireOp",EDGE,"E30");var subQ16=sQuery(id+"F6.wireOp",EDGE,"E29");var subQ17=sQuery(id+"F6.wireOp",EDGE,"E28");var subQ18=sQuery(id+"F6.wireOp",EDGE,"E27");var subQ19=sQuery(id+"F6.wireOp",EDGE,"E26");var subQ20=sQuery(id+"F6.wireOp",EDGE,"E25");var subQ21=sQuery(id+"F6.wireOp",EDGE,"E24");var subQ22=sQuery(id+"F6.wireOp",EDGE,"E23");var subQ23=sQuery(id+"F6.wireOp",EDGE,"E22");var subQ24=sQuery(id+"F6.wireOp",EDGE,"E21");var subQ25=sQuery(id+"F6.wireOp",EDGE,"E20");Q10=makeQuery(id+"F14.opBoolean","SPLIT",EDGE,{"disambiguationData":[TD([makeQuery(id+"F7.opExtrude","CAP_FACE",FACE,{"disambiguationData":[OSD([subQ25,subQ24,subQ23,subQ22,subQ21,subQ20,subQ19,subQ18,subQ17,subQ16,subQ15,subQ14,subQ13,subQ12,subQ11,subQ10,subQ9,subQ8,subQ7,subQ6,subQ5,subQ4,subQ3,subQ2,subQ1])],"isStart":false})])],"derivedFrom":makeQuery(id+"F5.opExtrude","CAP_EDGE",EDGE,{"disambiguationData":[OSD([subQ0])],"isStart":false})});}
            var Q11;
            {var subQ0=sQuery(id+"F6.wireOp",EDGE,"E43");Q11=makeQuery(id+"F14.opBoolean","SPLIT",EDGE,{"disambiguationData":[TD([makeQuery(id+"F1.opExtrude","SWEPT_FACE",FACE,{"disambiguationData":[OSD([sQuery(id+"F0.wireOp",EDGE,"E0")])]})])],"derivedFrom":makeQuery(id+"F10.opPattern","COPY",EDGE,{"derivedFrom":makeQuery(id+"F7.opExtrude","CAP_EDGE",EDGE,{"disambiguationData":[OSD([subQ0])],"isStart":true}),"instanceName":"7"})});}
            var Q12;
            {var subQ1=sQuery(id+"F6.wireOp",EDGE,"E43");Q12=makeQuery(id+"F14.opBoolean","SPLIT",EDGE,{"disambiguationData":[TD([makeQuery(id+"F1.opExtrude","SWEPT_FACE",FACE,{"disambiguationData":[OSD([sQuery(id+"F0.wireOp",EDGE,"E0")])]})])],"derivedFrom":makeQuery(id+"F10.opPattern","COPY",EDGE,{"derivedFrom":makeQuery(id+"F7.opExtrude","CAP_EDGE",EDGE,{"disambiguationData":[OSD([subQ1])],"isStart":false}),"instanceName":"7"})});}
            var Q13;
            {var subQ0=sQuery(id+"F6.wireOp",EDGE,"E44");var subQ1=sQuery(id+"F6.wireOp",EDGE,"E43");var subQ2=sQuery(id+"F6.wireOp",EDGE,"E42");var subQ3=sQuery(id+"F6.wireOp",EDGE,"E41");var subQ4=sQuery(id+"F6.wireOp",EDGE,"E40");var subQ5=sQuery(id+"F6.wireOp",EDGE,"E39");var subQ6=sQuery(id+"F6.wireOp",EDGE,"E38");var subQ7=sQuery(id+"F6.wireOp",EDGE,"E37");var subQ8=sQuery(id+"F6.wireOp",EDGE,"E36");var subQ9=sQuery(id+"F6.wireOp",EDGE,"E35");var subQ10=sQuery(id+"F6.wireOp",EDGE,"E34");var subQ11=sQuery(id+"F6.wireOp",EDGE,"E33");var subQ12=sQuery(id+"F6.wireOp",EDGE,"E32");var subQ13=sQuery(id+"F6.wireOp",EDGE,"E31");var subQ14=sQuery(id+"F6.wireOp",EDGE,"E30");var subQ15=sQuery(id+"F6.wireOp",EDGE,"E29");var subQ16=sQuery(id+"F6.wireOp",EDGE,"E28");var subQ17=sQuery(id+"F6.wireOp",EDGE,"E27");var subQ18=sQuery(id+"F6.wireOp",EDGE,"E26");var subQ19=sQuery(id+"F6.wireOp",EDGE,"E25");var subQ20=sQuery(id+"F6.wireOp",EDGE,"E24");var subQ21=sQuery(id+"F6.wireOp",EDGE,"E23");var subQ22=sQuery(id+"F6.wireOp",EDGE,"E22");var subQ23=sQuery(id+"F6.wireOp",EDGE,"E21");var subQ24=sQuery(id+"F6.wireOp",EDGE,"E20");var subQ25=sQuery(id+"F4.wireOp",EDGE,"E10");Q13=makeQuery(id+"F14.opBoolean","SPLIT",EDGE,{"disambiguationData":[TD([makeQuery(id+"F10.opPattern","COPY",FACE,{"derivedFrom":makeQuery(id+"F7.opExtrude","CAP_FACE",FACE,{"disambiguationData":[OSD([subQ24,subQ23,subQ22,subQ21,subQ20,subQ19,subQ18,subQ17,subQ16,subQ15,subQ14,subQ13,subQ12,subQ11,subQ10,subQ9,subQ8,subQ7,subQ6,subQ5,subQ4,subQ3,subQ2,subQ1,subQ0])],"isStart":true}),"instanceName":"6"})])],"derivedFrom":makeQuery(id+"F5.opExtrude","CAP_EDGE",EDGE,{"disambiguationData":[OSD([subQ25])],"isStart":false})});}
            var Q14;
            {var subQ0=sQuery(id+"F6.wireOp",EDGE,"E43");Q14=makeQuery(id+"F14.opBoolean","SPLIT",EDGE,{"disambiguationData":[TD([makeQuery(id+"F1.opExtrude","SWEPT_FACE",FACE,{"disambiguationData":[OSD([sQuery(id+"F0.wireOp",EDGE,"E0")])]})])],"derivedFrom":makeQuery(id+"F10.opPattern","COPY",EDGE,{"derivedFrom":makeQuery(id+"F7.opExtrude","CAP_EDGE",EDGE,{"disambiguationData":[OSD([subQ0])],"isStart":true}),"instanceName":"6"})});}
            var Q15;
            {var subQ0=sQuery(id+"F6.wireOp",EDGE,"E43");Q15=makeQuery(id+"F14.opBoolean","SPLIT",EDGE,{"disambiguationData":[TD([makeQuery(id+"F1.opExtrude","SWEPT_FACE",FACE,{"disambiguationData":[OSD([sQuery(id+"F0.wireOp",EDGE,"E0")])]})])],"derivedFrom":makeQuery(id+"F10.opPattern","COPY",EDGE,{"derivedFrom":makeQuery(id+"F7.opExtrude","CAP_EDGE",EDGE,{"disambiguationData":[OSD([subQ0])],"isStart":true}),"instanceName":"5"})});}
            var Q16;
            {var subQ0=sQuery(id+"F4.wireOp",EDGE,"E10");var subQ1=sQuery(id+"F6.wireOp",EDGE,"E44");var subQ2=sQuery(id+"F6.wireOp",EDGE,"E43");var subQ3=sQuery(id+"F6.wireOp",EDGE,"E42");var subQ4=sQuery(id+"F6.wireOp",EDGE,"E41");var subQ5=sQuery(id+"F6.wireOp",EDGE,"E40");var subQ6=sQuery(id+"F6.wireOp",EDGE,"E39");var subQ7=sQuery(id+"F6.wireOp",EDGE,"E38");var subQ8=sQuery(id+"F6.wireOp",EDGE,"E37");var subQ9=sQuery(id+"F6.wireOp",EDGE,"E36");var subQ10=sQuery(id+"F6.wireOp",EDGE,"E35");var subQ11=sQuery(id+"F6.wireOp",EDGE,"E34");var subQ12=sQuery(id+"F6.wireOp",EDGE,"E33");var subQ13=sQuery(id+"F6.wireOp",EDGE,"E32");var subQ14=sQuery(id+"F6.wireOp",EDGE,"E31");var subQ15=sQuery(id+"F6.wireOp",EDGE,"E30");var subQ16=sQuery(id+"F6.wireOp",EDGE,"E29");var subQ17=sQuery(id+"F6.wireOp",EDGE,"E28");var subQ18=sQuery(id+"F6.wireOp",EDGE,"E27");var subQ19=sQuery(id+"F6.wireOp",EDGE,"E26");var subQ20=sQuery(id+"F6.wireOp",EDGE,"E25");var subQ21=sQuery(id+"F6.wireOp",EDGE,"E24");var subQ22=sQuery(id+"F6.wireOp",EDGE,"E23");var subQ23=sQuery(id+"F6.wireOp",EDGE,"E22");var subQ24=sQuery(id+"F6.wireOp",EDGE,"E21");var subQ25=sQuery(id+"F6.wireOp",EDGE,"E20");Q16=makeQuery(id+"F14.opBoolean","SPLIT",EDGE,{"disambiguationData":[TD([makeQuery(id+"F10.opPattern","COPY",FACE,{"derivedFrom":makeQuery(id+"F7.opExtrude","CAP_FACE",FACE,{"disambiguationData":[OSD([subQ25,subQ24,subQ23,subQ22,subQ21,subQ20,subQ19,subQ18,subQ17,subQ16,subQ15,subQ14,subQ13,subQ12,subQ11,subQ10,subQ9,subQ8,subQ7,subQ6,subQ5,subQ4,subQ3,subQ2,subQ1])],"isStart":true}),"instanceName":"5"})])],"derivedFrom":makeQuery(id+"F5.opExtrude","CAP_EDGE",EDGE,{"disambiguationData":[OSD([subQ0])],"isStart":false})});}
            var Q17;
            {var subQ0=sQuery(id+"F6.wireOp",EDGE,"E43");Q17=makeQuery(id+"F14.opBoolean","SPLIT",EDGE,{"disambiguationData":[TD([makeQuery(id+"F1.opExtrude","SWEPT_FACE",FACE,{"disambiguationData":[OSD([sQuery(id+"F0.wireOp",EDGE,"E0")])]})])],"derivedFrom":makeQuery(id+"F10.opPattern","COPY",EDGE,{"derivedFrom":makeQuery(id+"F7.opExtrude","CAP_EDGE",EDGE,{"disambiguationData":[OSD([subQ0])],"isStart":false}),"instanceName":"6"})});}
            var Q18;
            {var subQ1=sQuery(id+"F6.wireOp",EDGE,"E43");Q18=makeQuery(id+"F14.opBoolean","SPLIT",EDGE,{"disambiguationData":[TD([makeQuery(id+"F1.opExtrude","SWEPT_FACE",FACE,{"disambiguationData":[OSD([sQuery(id+"F0.wireOp",EDGE,"E0")])]})])],"derivedFrom":makeQuery(id+"F10.opPattern","COPY",EDGE,{"derivedFrom":makeQuery(id+"F7.opExtrude","CAP_EDGE",EDGE,{"disambiguationData":[OSD([subQ1])],"isStart":true}),"instanceName":"4"})});}
            var Q19;
            {var subQ0=sQuery(id+"F6.wireOp",EDGE,"E44");var subQ1=sQuery(id+"F6.wireOp",EDGE,"E43");var subQ2=sQuery(id+"F6.wireOp",EDGE,"E42");var subQ3=sQuery(id+"F6.wireOp",EDGE,"E41");var subQ4=sQuery(id+"F6.wireOp",EDGE,"E40");var subQ5=sQuery(id+"F6.wireOp",EDGE,"E39");var subQ6=sQuery(id+"F6.wireOp",EDGE,"E38");var subQ7=sQuery(id+"F6.wireOp",EDGE,"E37");var subQ8=sQuery(id+"F6.wireOp",EDGE,"E36");var subQ9=sQuery(id+"F6.wireOp",EDGE,"E35");var subQ10=sQuery(id+"F6.wireOp",EDGE,"E34");var subQ11=sQuery(id+"F6.wireOp",EDGE,"E33");var subQ12=sQuery(id+"F6.wireOp",EDGE,"E32");var subQ13=sQuery(id+"F6.wireOp",EDGE,"E31");var subQ14=sQuery(id+"F6.wireOp",EDGE,"E30");var subQ15=sQuery(id+"F6.wireOp",EDGE,"E29");var subQ16=sQuery(id+"F6.wireOp",EDGE,"E28");var subQ17=sQuery(id+"F6.wireOp",EDGE,"E27");var subQ18=sQuery(id+"F6.wireOp",EDGE,"E26");var subQ19=sQuery(id+"F6.wireOp",EDGE,"E25");var subQ20=sQuery(id+"F6.wireOp",EDGE,"E24");var subQ21=sQuery(id+"F6.wireOp",EDGE,"E23");var subQ22=sQuery(id+"F6.wireOp",EDGE,"E22");var subQ23=sQuery(id+"F6.wireOp",EDGE,"E21");var subQ24=sQuery(id+"F6.wireOp",EDGE,"E20");var subQ25=sQuery(id+"F4.wireOp",EDGE,"E10");Q19=makeQuery(id+"F14.opBoolean","SPLIT",EDGE,{"disambiguationData":[TD([makeQuery(id+"F10.opPattern","COPY",FACE,{"derivedFrom":makeQuery(id+"F7.opExtrude","CAP_FACE",FACE,{"disambiguationData":[OSD([subQ24,subQ23,subQ22,subQ21,subQ20,subQ19,subQ18,subQ17,subQ16,subQ15,subQ14,subQ13,subQ12,subQ11,subQ10,subQ9,subQ8,subQ7,subQ6,subQ5,subQ4,subQ3,subQ2,subQ1,subQ0])],"isStart":true}),"instanceName":"4"})])],"derivedFrom":makeQuery(id+"F5.opExtrude","CAP_EDGE",EDGE,{"disambiguationData":[OSD([subQ25])],"isStart":false})});}
            var Q20;
            {var subQ1=sQuery(id+"F6.wireOp",EDGE,"E43");Q20=makeQuery(id+"F14.opBoolean","SPLIT",EDGE,{"disambiguationData":[TD([makeQuery(id+"F1.opExtrude","SWEPT_FACE",FACE,{"disambiguationData":[OSD([sQuery(id+"F0.wireOp",EDGE,"E0")])]})])],"derivedFrom":makeQuery(id+"F10.opPattern","COPY",EDGE,{"derivedFrom":makeQuery(id+"F7.opExtrude","CAP_EDGE",EDGE,{"disambiguationData":[OSD([subQ1])],"isStart":false}),"instanceName":"5"})});}
            var Q21;
            {var subQ0=sQuery(id+"F6.wireOp",EDGE,"E43");Q21=makeQuery(id+"F14.opBoolean","SPLIT",EDGE,{"disambiguationData":[TD([makeQuery(id+"F1.opExtrude","SWEPT_FACE",FACE,{"disambiguationData":[OSD([sQuery(id+"F0.wireOp",EDGE,"E0")])]})])],"derivedFrom":makeQuery(id+"F10.opPattern","COPY",EDGE,{"derivedFrom":makeQuery(id+"F7.opExtrude","CAP_EDGE",EDGE,{"disambiguationData":[OSD([subQ0])],"isStart":true}),"instanceName":"3"})});}
            var Q22;
            {var subQ0=sQuery(id+"F4.wireOp",EDGE,"E10");var subQ1=sQuery(id+"F6.wireOp",EDGE,"E44");var subQ2=sQuery(id+"F6.wireOp",EDGE,"E43");var subQ3=sQuery(id+"F6.wireOp",EDGE,"E42");var subQ4=sQuery(id+"F6.wireOp",EDGE,"E41");var subQ5=sQuery(id+"F6.wireOp",EDGE,"E40");var subQ6=sQuery(id+"F6.wireOp",EDGE,"E39");var subQ7=sQuery(id+"F6.wireOp",EDGE,"E38");var subQ8=sQuery(id+"F6.wireOp",EDGE,"E37");var subQ9=sQuery(id+"F6.wireOp",EDGE,"E36");var subQ10=sQuery(id+"F6.wireOp",EDGE,"E35");var subQ11=sQuery(id+"F6.wireOp",EDGE,"E34");var subQ12=sQuery(id+"F6.wireOp",EDGE,"E33");var subQ13=sQuery(id+"F6.wireOp",EDGE,"E32");var subQ14=sQuery(id+"F6.wireOp",EDGE,"E31");var subQ15=sQuery(id+"F6.wireOp",EDGE,"E30");var subQ16=sQuery(id+"F6.wireOp",EDGE,"E29");var subQ17=sQuery(id+"F6.wireOp",EDGE,"E28");var subQ18=sQuery(id+"F6.wireOp",EDGE,"E27");var subQ19=sQuery(id+"F6.wireOp",EDGE,"E26");var subQ20=sQuery(id+"F6.wireOp",EDGE,"E25");var subQ21=sQuery(id+"F6.wireOp",EDGE,"E24");var subQ22=sQuery(id+"F6.wireOp",EDGE,"E23");var subQ23=sQuery(id+"F6.wireOp",EDGE,"E22");var subQ24=sQuery(id+"F6.wireOp",EDGE,"E21");var subQ25=sQuery(id+"F6.wireOp",EDGE,"E20");Q22=makeQuery(id+"F14.opBoolean","SPLIT",EDGE,{"disambiguationData":[TD([makeQuery(id+"F10.opPattern","COPY",FACE,{"derivedFrom":makeQuery(id+"F7.opExtrude","CAP_FACE",FACE,{"disambiguationData":[OSD([subQ25,subQ24,subQ23,subQ22,subQ21,subQ20,subQ19,subQ18,subQ17,subQ16,subQ15,subQ14,subQ13,subQ12,subQ11,subQ10,subQ9,subQ8,subQ7,subQ6,subQ5,subQ4,subQ3,subQ2,subQ1])],"isStart":true}),"instanceName":"3"})])],"derivedFrom":makeQuery(id+"F5.opExtrude","CAP_EDGE",EDGE,{"disambiguationData":[OSD([subQ0])],"isStart":false})});}
            var Q23;
            {var subQ1=sQuery(id+"F6.wireOp",EDGE,"E43");Q23=makeQuery(id+"F14.opBoolean","SPLIT",EDGE,{"disambiguationData":[TD([makeQuery(id+"F1.opExtrude","SWEPT_FACE",FACE,{"disambiguationData":[OSD([sQuery(id+"F0.wireOp",EDGE,"E0")])]})])],"derivedFrom":makeQuery(id+"F10.opPattern","COPY",EDGE,{"derivedFrom":makeQuery(id+"F7.opExtrude","CAP_EDGE",EDGE,{"disambiguationData":[OSD([subQ1])],"isStart":false}),"instanceName":"4"})});}
            fillet(context, id + "F15", {"entities" : qUnion([Q0, Q1, Q2, Q3, Q4, Q5, Q6, Q7, Q8, Q9, Q10, Q11, Q12, Q13, Q14, Q15, Q16, Q17, Q18, Q19, Q20, Q21, Q22, Q23]), "radius" : 5 * mm, "tangentPropagation" : true, "allowEdgeOverflow" : false});
        }
        {
            var Q0;
            {var subQ0=sQuery(id+"F2.wireOp",EDGE,"E2");var subQ1=sQuery(id+"F6.wireOp",EDGE,"E44");var subQ2=sQuery(id+"F6.wireOp",EDGE,"E43");var subQ3=sQuery(id+"F6.wireOp",EDGE,"E42");var subQ4=sQuery(id+"F6.wireOp",EDGE,"E41");var subQ5=sQuery(id+"F6.wireOp",EDGE,"E40");var subQ6=sQuery(id+"F6.wireOp",EDGE,"E39");var subQ7=sQuery(id+"F6.wireOp",EDGE,"E38");var subQ8=sQuery(id+"F6.wireOp",EDGE,"E37");var subQ9=sQuery(id+"F6.wireOp",EDGE,"E36");var subQ10=sQuery(id+"F6.wireOp",EDGE,"E35");var subQ11=sQuery(id+"F6.wireOp",EDGE,"E34");var subQ12=sQuery(id+"F6.wireOp",EDGE,"E33");var subQ13=sQuery(id+"F6.wireOp",EDGE,"E32");var subQ14=sQuery(id+"F6.wireOp",EDGE,"E31");var subQ15=sQuery(id+"F6.wireOp",EDGE,"E30");var subQ16=sQuery(id+"F6.wireOp",EDGE,"E29");var subQ17=sQuery(id+"F6.wireOp",EDGE,"E28");var subQ18=sQuery(id+"F6.wireOp",EDGE,"E27");var subQ19=sQuery(id+"F6.wireOp",EDGE,"E26");var subQ20=sQuery(id+"F6.wireOp",EDGE,"E25");var subQ21=sQuery(id+"F6.wireOp",EDGE,"E24");var subQ22=sQuery(id+"F6.wireOp",EDGE,"E23");var subQ23=sQuery(id+"F6.wireOp",EDGE,"E22");var subQ24=sQuery(id+"F6.wireOp",EDGE,"E21");var subQ25=sQuery(id+"F6.wireOp",EDGE,"E20");Q0=makeQuery(id+"F14.opBoolean","SPLIT",EDGE,{"disambiguationData":[TD([makeQuery(id+"F10.opPattern","COPY",FACE,{"derivedFrom":makeQuery(id+"F7.opExtrude","CAP_FACE",FACE,{"disambiguationData":[OSD([subQ25,subQ24,subQ23,subQ22,subQ21,subQ20,subQ19,subQ18,subQ17,subQ16,subQ15,subQ14,subQ13,subQ12,subQ11,subQ10,subQ9,subQ8,subQ7,subQ6,subQ5,subQ4,subQ3,subQ2,subQ1])],"isStart":true}),"instanceName":"1"})])],"derivedFrom":makeQuery(id+"F3.opExtrude","CAP_EDGE",EDGE,{"disambiguationData":[OSD([subQ0])],"isStart":false})});}
            var Q1;
            {var subQ0=sQuery(id+"F6.wireOp",EDGE,"E20");Q1=makeQuery(id+"F14.opBoolean","SPLIT",EDGE,{"disambiguationData":[TD([makeQuery(id+"F1.opExtrude","SWEPT_FACE",FACE,{"disambiguationData":[OSD([sQuery(id+"F0.wireOp",EDGE,"E0")])]})])],"derivedFrom":makeQuery(id+"F10.opPattern","COPY",EDGE,{"derivedFrom":makeQuery(id+"F7.opExtrude","CAP_EDGE",EDGE,{"disambiguationData":[OSD([subQ0])],"isStart":false}),"instanceName":"2"})});}
            var Q2;
            {var subQ0=sQuery(id+"F6.wireOp",EDGE,"E20");Q2=makeQuery(id+"F14.opBoolean","SPLIT",EDGE,{"disambiguationData":[TD([makeQuery(id+"F1.opExtrude","SWEPT_FACE",FACE,{"disambiguationData":[OSD([sQuery(id+"F0.wireOp",EDGE,"E0")])]})])],"derivedFrom":makeQuery(id+"F10.opPattern","COPY",EDGE,{"derivedFrom":makeQuery(id+"F7.opExtrude","CAP_EDGE",EDGE,{"disambiguationData":[OSD([subQ0])],"isStart":true}),"instanceName":"1"})});}
            var Q3;
            {var subQ0=sQuery(id+"F6.wireOp",EDGE,"E20");Q3=makeQuery(id+"F14.opBoolean","SPLIT",EDGE,{"disambiguationData":[TD([makeQuery(id+"F1.opExtrude","SWEPT_FACE",FACE,{"disambiguationData":[OSD([sQuery(id+"F0.wireOp",EDGE,"E0")])]})])],"derivedFrom":makeQuery(id+"F10.opPattern","COPY",EDGE,{"derivedFrom":makeQuery(id+"F7.opExtrude","CAP_EDGE",EDGE,{"disambiguationData":[OSD([subQ0])],"isStart":true}),"instanceName":"2"})});}
            var Q4;
            {var subQ0=sQuery(id+"F2.wireOp",EDGE,"E2");var subQ1=sQuery(id+"F6.wireOp",EDGE,"E44");var subQ2=sQuery(id+"F6.wireOp",EDGE,"E43");var subQ3=sQuery(id+"F6.wireOp",EDGE,"E42");var subQ4=sQuery(id+"F6.wireOp",EDGE,"E41");var subQ5=sQuery(id+"F6.wireOp",EDGE,"E40");var subQ6=sQuery(id+"F6.wireOp",EDGE,"E39");var subQ7=sQuery(id+"F6.wireOp",EDGE,"E38");var subQ8=sQuery(id+"F6.wireOp",EDGE,"E37");var subQ9=sQuery(id+"F6.wireOp",EDGE,"E36");var subQ10=sQuery(id+"F6.wireOp",EDGE,"E35");var subQ11=sQuery(id+"F6.wireOp",EDGE,"E34");var subQ12=sQuery(id+"F6.wireOp",EDGE,"E33");var subQ13=sQuery(id+"F6.wireOp",EDGE,"E32");var subQ14=sQuery(id+"F6.wireOp",EDGE,"E31");var subQ15=sQuery(id+"F6.wireOp",EDGE,"E30");var subQ16=sQuery(id+"F6.wireOp",EDGE,"E29");var subQ17=sQuery(id+"F6.wireOp",EDGE,"E28");var subQ18=sQuery(id+"F6.wireOp",EDGE,"E27");var subQ19=sQuery(id+"F6.wireOp",EDGE,"E26");var subQ20=sQuery(id+"F6.wireOp",EDGE,"E25");var subQ21=sQuery(id+"F6.wireOp",EDGE,"E24");var subQ22=sQuery(id+"F6.wireOp",EDGE,"E23");var subQ23=sQuery(id+"F6.wireOp",EDGE,"E22");var subQ24=sQuery(id+"F6.wireOp",EDGE,"E21");var subQ25=sQuery(id+"F6.wireOp",EDGE,"E20");Q4=makeQuery(id+"F14.opBoolean","SPLIT",EDGE,{"disambiguationData":[TD([makeQuery(id+"F10.opPattern","COPY",FACE,{"derivedFrom":makeQuery(id+"F7.opExtrude","CAP_FACE",FACE,{"disambiguationData":[OSD([subQ25,subQ24,subQ23,subQ22,subQ21,subQ20,subQ19,subQ18,subQ17,subQ16,subQ15,subQ14,subQ13,subQ12,subQ11,subQ10,subQ9,subQ8,subQ7,subQ6,subQ5,subQ4,subQ3,subQ2,subQ1])],"isStart":true}),"instanceName":"2"})])],"derivedFrom":makeQuery(id+"F3.opExtrude","CAP_EDGE",EDGE,{"disambiguationData":[OSD([subQ0])],"isStart":false})});}
            var Q5;
            {var subQ0=sQuery(id+"F6.wireOp",EDGE,"E20");Q5=makeQuery(id+"F14.opBoolean","SPLIT",EDGE,{"disambiguationData":[TD([makeQuery(id+"F1.opExtrude","SWEPT_FACE",FACE,{"disambiguationData":[OSD([sQuery(id+"F0.wireOp",EDGE,"E0")])]})])],"derivedFrom":makeQuery(id+"F10.opPattern","COPY",EDGE,{"derivedFrom":makeQuery(id+"F7.opExtrude","CAP_EDGE",EDGE,{"disambiguationData":[OSD([subQ0])],"isStart":false}),"instanceName":"3"})});}
            var Q6;
            {var subQ0=sQuery(id+"F6.wireOp",EDGE,"E20");Q6=makeQuery(id+"F14.opBoolean","SPLIT",EDGE,{"disambiguationData":[TD([makeQuery(id+"F1.opExtrude","SWEPT_FACE",FACE,{"disambiguationData":[OSD([sQuery(id+"F0.wireOp",EDGE,"E0")])]})])],"derivedFrom":makeQuery(id+"F10.opPattern","COPY",EDGE,{"derivedFrom":makeQuery(id+"F7.opExtrude","CAP_EDGE",EDGE,{"disambiguationData":[OSD([subQ0])],"isStart":true}),"instanceName":"3"})});}
            var Q7;
            {var subQ0=sQuery(id+"F6.wireOp",EDGE,"E20");Q7=makeQuery(id+"F14.opBoolean","SPLIT",EDGE,{"disambiguationData":[TD([makeQuery(id+"F1.opExtrude","SWEPT_FACE",FACE,{"disambiguationData":[OSD([sQuery(id+"F0.wireOp",EDGE,"E0")])]})])],"derivedFrom":makeQuery(id+"F10.opPattern","COPY",EDGE,{"derivedFrom":makeQuery(id+"F7.opExtrude","CAP_EDGE",EDGE,{"disambiguationData":[OSD([subQ0])],"isStart":false}),"instanceName":"4"})});}
            var Q8;
            {var subQ0=sQuery(id+"F2.wireOp",EDGE,"E2");var subQ1=sQuery(id+"F6.wireOp",EDGE,"E44");var subQ2=sQuery(id+"F6.wireOp",EDGE,"E43");var subQ3=sQuery(id+"F6.wireOp",EDGE,"E42");var subQ4=sQuery(id+"F6.wireOp",EDGE,"E41");var subQ5=sQuery(id+"F6.wireOp",EDGE,"E40");var subQ6=sQuery(id+"F6.wireOp",EDGE,"E39");var subQ7=sQuery(id+"F6.wireOp",EDGE,"E38");var subQ8=sQuery(id+"F6.wireOp",EDGE,"E37");var subQ9=sQuery(id+"F6.wireOp",EDGE,"E36");var subQ10=sQuery(id+"F6.wireOp",EDGE,"E35");var subQ11=sQuery(id+"F6.wireOp",EDGE,"E34");var subQ12=sQuery(id+"F6.wireOp",EDGE,"E33");var subQ13=sQuery(id+"F6.wireOp",EDGE,"E32");var subQ14=sQuery(id+"F6.wireOp",EDGE,"E31");var subQ15=sQuery(id+"F6.wireOp",EDGE,"E30");var subQ16=sQuery(id+"F6.wireOp",EDGE,"E29");var subQ17=sQuery(id+"F6.wireOp",EDGE,"E28");var subQ18=sQuery(id+"F6.wireOp",EDGE,"E27");var subQ19=sQuery(id+"F6.wireOp",EDGE,"E26");var subQ20=sQuery(id+"F6.wireOp",EDGE,"E25");var subQ21=sQuery(id+"F6.wireOp",EDGE,"E24");var subQ22=sQuery(id+"F6.wireOp",EDGE,"E23");var subQ23=sQuery(id+"F6.wireOp",EDGE,"E22");var subQ24=sQuery(id+"F6.wireOp",EDGE,"E21");var subQ25=sQuery(id+"F6.wireOp",EDGE,"E20");Q8=makeQuery(id+"F14.opBoolean","SPLIT",EDGE,{"disambiguationData":[TD([makeQuery(id+"F10.opPattern","COPY",FACE,{"derivedFrom":makeQuery(id+"F7.opExtrude","CAP_FACE",FACE,{"disambiguationData":[OSD([subQ25,subQ24,subQ23,subQ22,subQ21,subQ20,subQ19,subQ18,subQ17,subQ16,subQ15,subQ14,subQ13,subQ12,subQ11,subQ10,subQ9,subQ8,subQ7,subQ6,subQ5,subQ4,subQ3,subQ2,subQ1])],"isStart":true}),"instanceName":"3"})])],"derivedFrom":makeQuery(id+"F3.opExtrude","CAP_EDGE",EDGE,{"disambiguationData":[OSD([subQ0])],"isStart":false})});}
            var Q9;
            {var subQ0=sQuery(id+"F6.wireOp",EDGE,"E20");Q9=makeQuery(id+"F14.opBoolean","SPLIT",EDGE,{"disambiguationData":[TD([makeQuery(id+"F1.opExtrude","SWEPT_FACE",FACE,{"disambiguationData":[OSD([sQuery(id+"F0.wireOp",EDGE,"E0")])]})])],"derivedFrom":makeQuery(id+"F10.opPattern","COPY",EDGE,{"derivedFrom":makeQuery(id+"F7.opExtrude","CAP_EDGE",EDGE,{"disambiguationData":[OSD([subQ0])],"isStart":true}),"instanceName":"4"})});}
            var Q10;
            {var subQ0=sQuery(id+"F2.wireOp",EDGE,"E2");var subQ1=sQuery(id+"F6.wireOp",EDGE,"E44");var subQ2=sQuery(id+"F6.wireOp",EDGE,"E43");var subQ3=sQuery(id+"F6.wireOp",EDGE,"E42");var subQ4=sQuery(id+"F6.wireOp",EDGE,"E41");var subQ5=sQuery(id+"F6.wireOp",EDGE,"E40");var subQ6=sQuery(id+"F6.wireOp",EDGE,"E39");var subQ7=sQuery(id+"F6.wireOp",EDGE,"E38");var subQ8=sQuery(id+"F6.wireOp",EDGE,"E37");var subQ9=sQuery(id+"F6.wireOp",EDGE,"E36");var subQ10=sQuery(id+"F6.wireOp",EDGE,"E35");var subQ11=sQuery(id+"F6.wireOp",EDGE,"E34");var subQ12=sQuery(id+"F6.wireOp",EDGE,"E33");var subQ13=sQuery(id+"F6.wireOp",EDGE,"E32");var subQ14=sQuery(id+"F6.wireOp",EDGE,"E31");var subQ15=sQuery(id+"F6.wireOp",EDGE,"E30");var subQ16=sQuery(id+"F6.wireOp",EDGE,"E29");var subQ17=sQuery(id+"F6.wireOp",EDGE,"E28");var subQ18=sQuery(id+"F6.wireOp",EDGE,"E27");var subQ19=sQuery(id+"F6.wireOp",EDGE,"E26");var subQ20=sQuery(id+"F6.wireOp",EDGE,"E25");var subQ21=sQuery(id+"F6.wireOp",EDGE,"E24");var subQ22=sQuery(id+"F6.wireOp",EDGE,"E23");var subQ23=sQuery(id+"F6.wireOp",EDGE,"E22");var subQ24=sQuery(id+"F6.wireOp",EDGE,"E21");var subQ25=sQuery(id+"F6.wireOp",EDGE,"E20");Q10=makeQuery(id+"F14.opBoolean","SPLIT",EDGE,{"disambiguationData":[TD([makeQuery(id+"F10.opPattern","COPY",FACE,{"derivedFrom":makeQuery(id+"F7.opExtrude","CAP_FACE",FACE,{"disambiguationData":[OSD([subQ25,subQ24,subQ23,subQ22,subQ21,subQ20,subQ19,subQ18,subQ17,subQ16,subQ15,subQ14,subQ13,subQ12,subQ11,subQ10,subQ9,subQ8,subQ7,subQ6,subQ5,subQ4,subQ3,subQ2,subQ1])],"isStart":true}),"instanceName":"4"})])],"derivedFrom":makeQuery(id+"F3.opExtrude","CAP_EDGE",EDGE,{"disambiguationData":[OSD([subQ0])],"isStart":false})});}
            var Q11;
            {var subQ0=sQuery(id+"F6.wireOp",EDGE,"E20");Q11=makeQuery(id+"F14.opBoolean","SPLIT",EDGE,{"disambiguationData":[TD([makeQuery(id+"F1.opExtrude","SWEPT_FACE",FACE,{"disambiguationData":[OSD([sQuery(id+"F0.wireOp",EDGE,"E0")])]})])],"derivedFrom":makeQuery(id+"F10.opPattern","COPY",EDGE,{"derivedFrom":makeQuery(id+"F7.opExtrude","CAP_EDGE",EDGE,{"disambiguationData":[OSD([subQ0])],"isStart":false}),"instanceName":"5"})});}
            var Q12;
            {var subQ0=sQuery(id+"F6.wireOp",EDGE,"E20");Q12=makeQuery(id+"F14.opBoolean","SPLIT",EDGE,{"disambiguationData":[TD([makeQuery(id+"F1.opExtrude","SWEPT_FACE",FACE,{"disambiguationData":[OSD([sQuery(id+"F0.wireOp",EDGE,"E0")])]})])],"derivedFrom":makeQuery(id+"F10.opPattern","COPY",EDGE,{"derivedFrom":makeQuery(id+"F7.opExtrude","CAP_EDGE",EDGE,{"disambiguationData":[OSD([subQ0])],"isStart":true}),"instanceName":"5"})});}
            var Q13;
            {var subQ0=sQuery(id+"F2.wireOp",EDGE,"E2");var subQ1=sQuery(id+"F6.wireOp",EDGE,"E44");var subQ2=sQuery(id+"F6.wireOp",EDGE,"E43");var subQ3=sQuery(id+"F6.wireOp",EDGE,"E42");var subQ4=sQuery(id+"F6.wireOp",EDGE,"E41");var subQ5=sQuery(id+"F6.wireOp",EDGE,"E40");var subQ6=sQuery(id+"F6.wireOp",EDGE,"E39");var subQ7=sQuery(id+"F6.wireOp",EDGE,"E38");var subQ8=sQuery(id+"F6.wireOp",EDGE,"E37");var subQ9=sQuery(id+"F6.wireOp",EDGE,"E36");var subQ10=sQuery(id+"F6.wireOp",EDGE,"E35");var subQ11=sQuery(id+"F6.wireOp",EDGE,"E34");var subQ12=sQuery(id+"F6.wireOp",EDGE,"E33");var subQ13=sQuery(id+"F6.wireOp",EDGE,"E32");var subQ14=sQuery(id+"F6.wireOp",EDGE,"E31");var subQ15=sQuery(id+"F6.wireOp",EDGE,"E30");var subQ16=sQuery(id+"F6.wireOp",EDGE,"E29");var subQ17=sQuery(id+"F6.wireOp",EDGE,"E28");var subQ18=sQuery(id+"F6.wireOp",EDGE,"E27");var subQ19=sQuery(id+"F6.wireOp",EDGE,"E26");var subQ20=sQuery(id+"F6.wireOp",EDGE,"E25");var subQ21=sQuery(id+"F6.wireOp",EDGE,"E24");var subQ22=sQuery(id+"F6.wireOp",EDGE,"E23");var subQ23=sQuery(id+"F6.wireOp",EDGE,"E22");var subQ24=sQuery(id+"F6.wireOp",EDGE,"E21");var subQ25=sQuery(id+"F6.wireOp",EDGE,"E20");Q13=makeQuery(id+"F14.opBoolean","SPLIT",EDGE,{"disambiguationData":[TD([makeQuery(id+"F10.opPattern","COPY",FACE,{"derivedFrom":makeQuery(id+"F7.opExtrude","CAP_FACE",FACE,{"disambiguationData":[OSD([subQ25,subQ24,subQ23,subQ22,subQ21,subQ20,subQ19,subQ18,subQ17,subQ16,subQ15,subQ14,subQ13,subQ12,subQ11,subQ10,subQ9,subQ8,subQ7,subQ6,subQ5,subQ4,subQ3,subQ2,subQ1])],"isStart":true}),"instanceName":"5"})])],"derivedFrom":makeQuery(id+"F3.opExtrude","CAP_EDGE",EDGE,{"disambiguationData":[OSD([subQ0])],"isStart":false})});}
            var Q14;
            {var subQ0=sQuery(id+"F6.wireOp",EDGE,"E20");Q14=makeQuery(id+"F14.opBoolean","SPLIT",EDGE,{"disambiguationData":[TD([makeQuery(id+"F1.opExtrude","SWEPT_FACE",FACE,{"disambiguationData":[OSD([sQuery(id+"F0.wireOp",EDGE,"E0")])]})])],"derivedFrom":makeQuery(id+"F10.opPattern","COPY",EDGE,{"derivedFrom":makeQuery(id+"F7.opExtrude","CAP_EDGE",EDGE,{"disambiguationData":[OSD([subQ0])],"isStart":false}),"instanceName":"6"})});}
            var Q15;
            {var subQ0=sQuery(id+"F6.wireOp",EDGE,"E20");Q15=makeQuery(id+"F14.opBoolean","SPLIT",EDGE,{"disambiguationData":[TD([makeQuery(id+"F1.opExtrude","SWEPT_FACE",FACE,{"disambiguationData":[OSD([sQuery(id+"F0.wireOp",EDGE,"E0")])]})])],"derivedFrom":makeQuery(id+"F10.opPattern","COPY",EDGE,{"derivedFrom":makeQuery(id+"F7.opExtrude","CAP_EDGE",EDGE,{"disambiguationData":[OSD([subQ0])],"isStart":true}),"instanceName":"6"})});}
            var Q16;
            {var subQ0=sQuery(id+"F2.wireOp",EDGE,"E2");var subQ1=sQuery(id+"F6.wireOp",EDGE,"E44");var subQ2=sQuery(id+"F6.wireOp",EDGE,"E43");var subQ3=sQuery(id+"F6.wireOp",EDGE,"E42");var subQ4=sQuery(id+"F6.wireOp",EDGE,"E41");var subQ5=sQuery(id+"F6.wireOp",EDGE,"E40");var subQ6=sQuery(id+"F6.wireOp",EDGE,"E39");var subQ7=sQuery(id+"F6.wireOp",EDGE,"E38");var subQ8=sQuery(id+"F6.wireOp",EDGE,"E37");var subQ9=sQuery(id+"F6.wireOp",EDGE,"E36");var subQ10=sQuery(id+"F6.wireOp",EDGE,"E35");var subQ11=sQuery(id+"F6.wireOp",EDGE,"E34");var subQ12=sQuery(id+"F6.wireOp",EDGE,"E33");var subQ13=sQuery(id+"F6.wireOp",EDGE,"E32");var subQ14=sQuery(id+"F6.wireOp",EDGE,"E31");var subQ15=sQuery(id+"F6.wireOp",EDGE,"E30");var subQ16=sQuery(id+"F6.wireOp",EDGE,"E29");var subQ17=sQuery(id+"F6.wireOp",EDGE,"E28");var subQ18=sQuery(id+"F6.wireOp",EDGE,"E27");var subQ19=sQuery(id+"F6.wireOp",EDGE,"E26");var subQ20=sQuery(id+"F6.wireOp",EDGE,"E25");var subQ21=sQuery(id+"F6.wireOp",EDGE,"E24");var subQ22=sQuery(id+"F6.wireOp",EDGE,"E23");var subQ23=sQuery(id+"F6.wireOp",EDGE,"E22");var subQ24=sQuery(id+"F6.wireOp",EDGE,"E21");var subQ25=sQuery(id+"F6.wireOp",EDGE,"E20");Q16=makeQuery(id+"F14.opBoolean","SPLIT",EDGE,{"disambiguationData":[TD([makeQuery(id+"F10.opPattern","COPY",FACE,{"derivedFrom":makeQuery(id+"F7.opExtrude","CAP_FACE",FACE,{"disambiguationData":[OSD([subQ25,subQ24,subQ23,subQ22,subQ21,subQ20,subQ19,subQ18,subQ17,subQ16,subQ15,subQ14,subQ13,subQ12,subQ11,subQ10,subQ9,subQ8,subQ7,subQ6,subQ5,subQ4,subQ3,subQ2,subQ1])],"isStart":true}),"instanceName":"6"})])],"derivedFrom":makeQuery(id+"F3.opExtrude","CAP_EDGE",EDGE,{"disambiguationData":[OSD([subQ0])],"isStart":false})});}
            var Q17;
            {var subQ0=sQuery(id+"F6.wireOp",EDGE,"E20");Q17=makeQuery(id+"F14.opBoolean","SPLIT",EDGE,{"disambiguationData":[TD([makeQuery(id+"F1.opExtrude","SWEPT_FACE",FACE,{"disambiguationData":[OSD([sQuery(id+"F0.wireOp",EDGE,"E0")])]})])],"derivedFrom":makeQuery(id+"F10.opPattern","COPY",EDGE,{"derivedFrom":makeQuery(id+"F7.opExtrude","CAP_EDGE",EDGE,{"disambiguationData":[OSD([subQ0])],"isStart":false}),"instanceName":"7"})});}
            var Q18;
            {var subQ0=sQuery(id+"F6.wireOp",EDGE,"E20");Q18=makeQuery(id+"F14.opBoolean","SPLIT",EDGE,{"disambiguationData":[TD([makeQuery(id+"F1.opExtrude","SWEPT_FACE",FACE,{"disambiguationData":[OSD([sQuery(id+"F0.wireOp",EDGE,"E0")])]})])],"derivedFrom":makeQuery(id+"F10.opPattern","COPY",EDGE,{"derivedFrom":makeQuery(id+"F7.opExtrude","CAP_EDGE",EDGE,{"disambiguationData":[OSD([subQ0])],"isStart":true}),"instanceName":"7"})});}
            var Q19;
            {var subQ0=sQuery(id+"F2.wireOp",EDGE,"E2");var subQ1=sQuery(id+"F6.wireOp",EDGE,"E44");var subQ2=sQuery(id+"F6.wireOp",EDGE,"E43");var subQ3=sQuery(id+"F6.wireOp",EDGE,"E42");var subQ4=sQuery(id+"F6.wireOp",EDGE,"E41");var subQ5=sQuery(id+"F6.wireOp",EDGE,"E40");var subQ6=sQuery(id+"F6.wireOp",EDGE,"E39");var subQ7=sQuery(id+"F6.wireOp",EDGE,"E38");var subQ8=sQuery(id+"F6.wireOp",EDGE,"E37");var subQ9=sQuery(id+"F6.wireOp",EDGE,"E36");var subQ10=sQuery(id+"F6.wireOp",EDGE,"E35");var subQ11=sQuery(id+"F6.wireOp",EDGE,"E34");var subQ12=sQuery(id+"F6.wireOp",EDGE,"E33");var subQ13=sQuery(id+"F6.wireOp",EDGE,"E32");var subQ14=sQuery(id+"F6.wireOp",EDGE,"E31");var subQ15=sQuery(id+"F6.wireOp",EDGE,"E30");var subQ16=sQuery(id+"F6.wireOp",EDGE,"E29");var subQ17=sQuery(id+"F6.wireOp",EDGE,"E28");var subQ18=sQuery(id+"F6.wireOp",EDGE,"E27");var subQ19=sQuery(id+"F6.wireOp",EDGE,"E26");var subQ20=sQuery(id+"F6.wireOp",EDGE,"E25");var subQ21=sQuery(id+"F6.wireOp",EDGE,"E24");var subQ22=sQuery(id+"F6.wireOp",EDGE,"E23");var subQ23=sQuery(id+"F6.wireOp",EDGE,"E22");var subQ24=sQuery(id+"F6.wireOp",EDGE,"E21");var subQ25=sQuery(id+"F6.wireOp",EDGE,"E20");Q19=makeQuery(id+"F14.opBoolean","SPLIT",EDGE,{"disambiguationData":[TD([makeQuery(id+"F7.opExtrude","CAP_FACE",FACE,{"disambiguationData":[OSD([subQ25,subQ24,subQ23,subQ22,subQ21,subQ20,subQ19,subQ18,subQ17,subQ16,subQ15,subQ14,subQ13,subQ12,subQ11,subQ10,subQ9,subQ8,subQ7,subQ6,subQ5,subQ4,subQ3,subQ2,subQ1])],"isStart":false})])],"derivedFrom":makeQuery(id+"F3.opExtrude","CAP_EDGE",EDGE,{"disambiguationData":[OSD([subQ0])],"isStart":false})});}
            var Q20;
            {var subQ0=sQuery(id+"F6.wireOp",EDGE,"E20");Q20=makeQuery(id+"F14.opBoolean","SPLIT",EDGE,{"disambiguationData":[TD([makeQuery(id+"F1.opExtrude","SWEPT_FACE",FACE,{"disambiguationData":[OSD([sQuery(id+"F0.wireOp",EDGE,"E0")])]})])],"derivedFrom":makeQuery(id+"F7.opExtrude","CAP_EDGE",EDGE,{"disambiguationData":[OSD([subQ0])],"isStart":false})});}
            var Q21;
            {var subQ0=sQuery(id+"F6.wireOp",EDGE,"E20");Q21=makeQuery(id+"F14.opBoolean","SPLIT",EDGE,{"disambiguationData":[TD([makeQuery(id+"F1.opExtrude","SWEPT_FACE",FACE,{"disambiguationData":[OSD([sQuery(id+"F0.wireOp",EDGE,"E0")])]})])],"derivedFrom":makeQuery(id+"F7.opExtrude","CAP_EDGE",EDGE,{"disambiguationData":[OSD([subQ0])],"isStart":true})});}
            var Q22;
            {var subQ0=sQuery(id+"F2.wireOp",EDGE,"E2");var subQ1=sQuery(id+"F6.wireOp",EDGE,"E44");var subQ2=sQuery(id+"F6.wireOp",EDGE,"E43");var subQ3=sQuery(id+"F6.wireOp",EDGE,"E42");var subQ4=sQuery(id+"F6.wireOp",EDGE,"E41");var subQ5=sQuery(id+"F6.wireOp",EDGE,"E40");var subQ6=sQuery(id+"F6.wireOp",EDGE,"E39");var subQ7=sQuery(id+"F6.wireOp",EDGE,"E38");var subQ8=sQuery(id+"F6.wireOp",EDGE,"E37");var subQ9=sQuery(id+"F6.wireOp",EDGE,"E36");var subQ10=sQuery(id+"F6.wireOp",EDGE,"E35");var subQ11=sQuery(id+"F6.wireOp",EDGE,"E34");var subQ12=sQuery(id+"F6.wireOp",EDGE,"E33");var subQ13=sQuery(id+"F6.wireOp",EDGE,"E32");var subQ14=sQuery(id+"F6.wireOp",EDGE,"E31");var subQ15=sQuery(id+"F6.wireOp",EDGE,"E30");var subQ16=sQuery(id+"F6.wireOp",EDGE,"E29");var subQ17=sQuery(id+"F6.wireOp",EDGE,"E28");var subQ18=sQuery(id+"F6.wireOp",EDGE,"E27");var subQ19=sQuery(id+"F6.wireOp",EDGE,"E26");var subQ20=sQuery(id+"F6.wireOp",EDGE,"E25");var subQ21=sQuery(id+"F6.wireOp",EDGE,"E24");var subQ22=sQuery(id+"F6.wireOp",EDGE,"E23");var subQ23=sQuery(id+"F6.wireOp",EDGE,"E22");var subQ24=sQuery(id+"F6.wireOp",EDGE,"E21");var subQ25=sQuery(id+"F6.wireOp",EDGE,"E20");Q22=makeQuery(id+"F14.opBoolean","SPLIT",EDGE,{"disambiguationData":[TD([makeQuery(id+"F7.opExtrude","CAP_FACE",FACE,{"disambiguationData":[OSD([subQ25,subQ24,subQ23,subQ22,subQ21,subQ20,subQ19,subQ18,subQ17,subQ16,subQ15,subQ14,subQ13,subQ12,subQ11,subQ10,subQ9,subQ8,subQ7,subQ6,subQ5,subQ4,subQ3,subQ2,subQ1])],"isStart":true})])],"derivedFrom":makeQuery(id+"F3.opExtrude","CAP_EDGE",EDGE,{"disambiguationData":[OSD([subQ0])],"isStart":false})});}
            var Q23;
            {var subQ0=sQuery(id+"F6.wireOp",EDGE,"E20");Q23=makeQuery(id+"F14.opBoolean","SPLIT",EDGE,{"disambiguationData":[TD([makeQuery(id+"F1.opExtrude","SWEPT_FACE",FACE,{"disambiguationData":[OSD([sQuery(id+"F0.wireOp",EDGE,"E0")])]})])],"derivedFrom":makeQuery(id+"F10.opPattern","COPY",EDGE,{"derivedFrom":makeQuery(id+"F7.opExtrude","CAP_EDGE",EDGE,{"disambiguationData":[OSD([subQ0])],"isStart":false}),"instanceName":"1"})});}
            fillet(context, id + "F16", {"entities" : qUnion([Q0, Q1, Q2, Q3, Q4, Q5, Q6, Q7, Q8, Q9, Q10, Q11, Q12, Q13, Q14, Q15, Q16, Q17, Q18, Q19, Q20, Q21, Q22, Q23]), "radius" : 5 * mm, "tangentPropagation" : true, "allowEdgeOverflow" : false});
        }
        {
            var Q0;
            Q0=makeQuery(id+"F10.opPattern","COPY",EDGE,{"derivedFrom":makeQuery(id+"F9.boolean.opBoolean","INTERSECT",EDGE,{"derivedFrom":[makeQuery(id+"F7.opExtrude","CAP_FACE",FACE,{"disambiguationData":[OSD([sQuery(id+"F6.wireOp",EDGE,"E20"),sQuery(id+"F6.wireOp",EDGE,"E21"),sQuery(id+"F6.wireOp",EDGE,"E22"),sQuery(id+"F6.wireOp",EDGE,"E23"),sQuery(id+"F6.wireOp",EDGE,"E24"),sQuery(id+"F6.wireOp",EDGE,"E25"),sQuery(id+"F6.wireOp",EDGE,"E26"),sQuery(id+"F6.wireOp",EDGE,"E27"),sQuery(id+"F6.wireOp",EDGE,"E28"),sQuery(id+"F6.wireOp",EDGE,"E29"),sQuery(id+"F6.wireOp",EDGE,"E30"),sQuery(id+"F6.wireOp",EDGE,"E31"),sQuery(id+"F6.wireOp",EDGE,"E32"),sQuery(id+"F6.wireOp",EDGE,"E33"),sQuery(id+"F6.wireOp",EDGE,"E34"),sQuery(id+"F6.wireOp",EDGE,"E35"),sQuery(id+"F6.wireOp",EDGE,"E36"),sQuery(id+"F6.wireOp",EDGE,"E37"),sQuery(id+"F6.wireOp",EDGE,"E38"),sQuery(id+"F6.wireOp",EDGE,"E39"),sQuery(id+"F6.wireOp",EDGE,"E40"),sQuery(id+"F6.wireOp",EDGE,"E41"),sQuery(id+"F6.wireOp",EDGE,"E42"),sQuery(id+"F6.wireOp",EDGE,"E43"),sQuery(id+"F6.wireOp",EDGE,"E44")])],"isStart":false}),makeQuery(id+"F9.opExtrude","SWEPT_FACE",FACE,{"disambiguationData":[OSD([sQuery(id+"F8.wireOp",EDGE,"E45")])]})]}),"instanceName":"3"});
            var Q1;
            Q1=makeQuery(id+"F10.opPattern","COPY",EDGE,{"derivedFrom":makeQuery(id+"F9.boolean.opBoolean","INTERSECT",EDGE,{"derivedFrom":[makeQuery(id+"F7.opExtrude","CAP_FACE",FACE,{"disambiguationData":[OSD([sQuery(id+"F6.wireOp",EDGE,"E20"),sQuery(id+"F6.wireOp",EDGE,"E21"),sQuery(id+"F6.wireOp",EDGE,"E22"),sQuery(id+"F6.wireOp",EDGE,"E23"),sQuery(id+"F6.wireOp",EDGE,"E24"),sQuery(id+"F6.wireOp",EDGE,"E25"),sQuery(id+"F6.wireOp",EDGE,"E26"),sQuery(id+"F6.wireOp",EDGE,"E27"),sQuery(id+"F6.wireOp",EDGE,"E28"),sQuery(id+"F6.wireOp",EDGE,"E29"),sQuery(id+"F6.wireOp",EDGE,"E30"),sQuery(id+"F6.wireOp",EDGE,"E31"),sQuery(id+"F6.wireOp",EDGE,"E32"),sQuery(id+"F6.wireOp",EDGE,"E33"),sQuery(id+"F6.wireOp",EDGE,"E34"),sQuery(id+"F6.wireOp",EDGE,"E35"),sQuery(id+"F6.wireOp",EDGE,"E36"),sQuery(id+"F6.wireOp",EDGE,"E37"),sQuery(id+"F6.wireOp",EDGE,"E38"),sQuery(id+"F6.wireOp",EDGE,"E39"),sQuery(id+"F6.wireOp",EDGE,"E40"),sQuery(id+"F6.wireOp",EDGE,"E41"),sQuery(id+"F6.wireOp",EDGE,"E42"),sQuery(id+"F6.wireOp",EDGE,"E43"),sQuery(id+"F6.wireOp",EDGE,"E44")])],"isStart":true}),makeQuery(id+"F9.opExtrude","SWEPT_FACE",FACE,{"disambiguationData":[OSD([sQuery(id+"F8.wireOp",EDGE,"E45")])]})]}),"instanceName":"2"});
            var Q2;
            Q2=makeQuery(id+"F10.opPattern","COPY",EDGE,{"derivedFrom":makeQuery(id+"F9.boolean.opBoolean","INTERSECT",EDGE,{"derivedFrom":[makeQuery(id+"F7.opExtrude","CAP_FACE",FACE,{"disambiguationData":[OSD([sQuery(id+"F6.wireOp",EDGE,"E20"),sQuery(id+"F6.wireOp",EDGE,"E21"),sQuery(id+"F6.wireOp",EDGE,"E22"),sQuery(id+"F6.wireOp",EDGE,"E23"),sQuery(id+"F6.wireOp",EDGE,"E24"),sQuery(id+"F6.wireOp",EDGE,"E25"),sQuery(id+"F6.wireOp",EDGE,"E26"),sQuery(id+"F6.wireOp",EDGE,"E27"),sQuery(id+"F6.wireOp",EDGE,"E28"),sQuery(id+"F6.wireOp",EDGE,"E29"),sQuery(id+"F6.wireOp",EDGE,"E30"),sQuery(id+"F6.wireOp",EDGE,"E31"),sQuery(id+"F6.wireOp",EDGE,"E32"),sQuery(id+"F6.wireOp",EDGE,"E33"),sQuery(id+"F6.wireOp",EDGE,"E34"),sQuery(id+"F6.wireOp",EDGE,"E35"),sQuery(id+"F6.wireOp",EDGE,"E36"),sQuery(id+"F6.wireOp",EDGE,"E37"),sQuery(id+"F6.wireOp",EDGE,"E38"),sQuery(id+"F6.wireOp",EDGE,"E39"),sQuery(id+"F6.wireOp",EDGE,"E40"),sQuery(id+"F6.wireOp",EDGE,"E41"),sQuery(id+"F6.wireOp",EDGE,"E42"),sQuery(id+"F6.wireOp",EDGE,"E43"),sQuery(id+"F6.wireOp",EDGE,"E44")])],"isStart":false}),makeQuery(id+"F9.opExtrude","SWEPT_FACE",FACE,{"disambiguationData":[OSD([sQuery(id+"F8.wireOp",EDGE,"E45")])]})]}),"instanceName":"2"});
            var Q3;
            Q3=makeQuery(id+"F10.opPattern","COPY",EDGE,{"derivedFrom":makeQuery(id+"F9.boolean.opBoolean","INTERSECT",EDGE,{"derivedFrom":[makeQuery(id+"F7.opExtrude","CAP_FACE",FACE,{"disambiguationData":[OSD([sQuery(id+"F6.wireOp",EDGE,"E20"),sQuery(id+"F6.wireOp",EDGE,"E21"),sQuery(id+"F6.wireOp",EDGE,"E22"),sQuery(id+"F6.wireOp",EDGE,"E23"),sQuery(id+"F6.wireOp",EDGE,"E24"),sQuery(id+"F6.wireOp",EDGE,"E25"),sQuery(id+"F6.wireOp",EDGE,"E26"),sQuery(id+"F6.wireOp",EDGE,"E27"),sQuery(id+"F6.wireOp",EDGE,"E28"),sQuery(id+"F6.wireOp",EDGE,"E29"),sQuery(id+"F6.wireOp",EDGE,"E30"),sQuery(id+"F6.wireOp",EDGE,"E31"),sQuery(id+"F6.wireOp",EDGE,"E32"),sQuery(id+"F6.wireOp",EDGE,"E33"),sQuery(id+"F6.wireOp",EDGE,"E34"),sQuery(id+"F6.wireOp",EDGE,"E35"),sQuery(id+"F6.wireOp",EDGE,"E36"),sQuery(id+"F6.wireOp",EDGE,"E37"),sQuery(id+"F6.wireOp",EDGE,"E38"),sQuery(id+"F6.wireOp",EDGE,"E39"),sQuery(id+"F6.wireOp",EDGE,"E40"),sQuery(id+"F6.wireOp",EDGE,"E41"),sQuery(id+"F6.wireOp",EDGE,"E42"),sQuery(id+"F6.wireOp",EDGE,"E43"),sQuery(id+"F6.wireOp",EDGE,"E44")])],"isStart":true}),makeQuery(id+"F9.opExtrude","SWEPT_FACE",FACE,{"disambiguationData":[OSD([sQuery(id+"F8.wireOp",EDGE,"E45")])]})]}),"instanceName":"1"});
            var Q4;
            Q4=makeQuery(id+"F10.opPattern","COPY",EDGE,{"derivedFrom":makeQuery(id+"F9.boolean.opBoolean","INTERSECT",EDGE,{"derivedFrom":[makeQuery(id+"F7.opExtrude","CAP_FACE",FACE,{"disambiguationData":[OSD([sQuery(id+"F6.wireOp",EDGE,"E20"),sQuery(id+"F6.wireOp",EDGE,"E21"),sQuery(id+"F6.wireOp",EDGE,"E22"),sQuery(id+"F6.wireOp",EDGE,"E23"),sQuery(id+"F6.wireOp",EDGE,"E24"),sQuery(id+"F6.wireOp",EDGE,"E25"),sQuery(id+"F6.wireOp",EDGE,"E26"),sQuery(id+"F6.wireOp",EDGE,"E27"),sQuery(id+"F6.wireOp",EDGE,"E28"),sQuery(id+"F6.wireOp",EDGE,"E29"),sQuery(id+"F6.wireOp",EDGE,"E30"),sQuery(id+"F6.wireOp",EDGE,"E31"),sQuery(id+"F6.wireOp",EDGE,"E32"),sQuery(id+"F6.wireOp",EDGE,"E33"),sQuery(id+"F6.wireOp",EDGE,"E34"),sQuery(id+"F6.wireOp",EDGE,"E35"),sQuery(id+"F6.wireOp",EDGE,"E36"),sQuery(id+"F6.wireOp",EDGE,"E37"),sQuery(id+"F6.wireOp",EDGE,"E38"),sQuery(id+"F6.wireOp",EDGE,"E39"),sQuery(id+"F6.wireOp",EDGE,"E40"),sQuery(id+"F6.wireOp",EDGE,"E41"),sQuery(id+"F6.wireOp",EDGE,"E42"),sQuery(id+"F6.wireOp",EDGE,"E43"),sQuery(id+"F6.wireOp",EDGE,"E44")])],"isStart":false}),makeQuery(id+"F9.opExtrude","SWEPT_FACE",FACE,{"disambiguationData":[OSD([sQuery(id+"F8.wireOp",EDGE,"E45")])]})]}),"instanceName":"1"});
            var Q5;
            Q5=makeQuery(id+"F9.boolean.opBoolean","INTERSECT",EDGE,{"derivedFrom":[makeQuery(id+"F7.opExtrude","CAP_FACE",FACE,{"disambiguationData":[OSD([sQuery(id+"F6.wireOp",EDGE,"E20"),sQuery(id+"F6.wireOp",EDGE,"E21"),sQuery(id+"F6.wireOp",EDGE,"E22"),sQuery(id+"F6.wireOp",EDGE,"E23"),sQuery(id+"F6.wireOp",EDGE,"E24"),sQuery(id+"F6.wireOp",EDGE,"E25"),sQuery(id+"F6.wireOp",EDGE,"E26"),sQuery(id+"F6.wireOp",EDGE,"E27"),sQuery(id+"F6.wireOp",EDGE,"E28"),sQuery(id+"F6.wireOp",EDGE,"E29"),sQuery(id+"F6.wireOp",EDGE,"E30"),sQuery(id+"F6.wireOp",EDGE,"E31"),sQuery(id+"F6.wireOp",EDGE,"E32"),sQuery(id+"F6.wireOp",EDGE,"E33"),sQuery(id+"F6.wireOp",EDGE,"E34"),sQuery(id+"F6.wireOp",EDGE,"E35"),sQuery(id+"F6.wireOp",EDGE,"E36"),sQuery(id+"F6.wireOp",EDGE,"E37"),sQuery(id+"F6.wireOp",EDGE,"E38"),sQuery(id+"F6.wireOp",EDGE,"E39"),sQuery(id+"F6.wireOp",EDGE,"E40"),sQuery(id+"F6.wireOp",EDGE,"E41"),sQuery(id+"F6.wireOp",EDGE,"E42"),sQuery(id+"F6.wireOp",EDGE,"E43"),sQuery(id+"F6.wireOp",EDGE,"E44")])],"isStart":true}),makeQuery(id+"F9.opExtrude","SWEPT_FACE",FACE,{"disambiguationData":[OSD([sQuery(id+"F8.wireOp",EDGE,"E45")])]})]});
            var Q6;
            Q6=makeQuery(id+"F9.boolean.opBoolean","INTERSECT",EDGE,{"derivedFrom":[makeQuery(id+"F7.opExtrude","CAP_FACE",FACE,{"disambiguationData":[OSD([sQuery(id+"F6.wireOp",EDGE,"E20"),sQuery(id+"F6.wireOp",EDGE,"E21"),sQuery(id+"F6.wireOp",EDGE,"E22"),sQuery(id+"F6.wireOp",EDGE,"E23"),sQuery(id+"F6.wireOp",EDGE,"E24"),sQuery(id+"F6.wireOp",EDGE,"E25"),sQuery(id+"F6.wireOp",EDGE,"E26"),sQuery(id+"F6.wireOp",EDGE,"E27"),sQuery(id+"F6.wireOp",EDGE,"E28"),sQuery(id+"F6.wireOp",EDGE,"E29"),sQuery(id+"F6.wireOp",EDGE,"E30"),sQuery(id+"F6.wireOp",EDGE,"E31"),sQuery(id+"F6.wireOp",EDGE,"E32"),sQuery(id+"F6.wireOp",EDGE,"E33"),sQuery(id+"F6.wireOp",EDGE,"E34"),sQuery(id+"F6.wireOp",EDGE,"E35"),sQuery(id+"F6.wireOp",EDGE,"E36"),sQuery(id+"F6.wireOp",EDGE,"E37"),sQuery(id+"F6.wireOp",EDGE,"E38"),sQuery(id+"F6.wireOp",EDGE,"E39"),sQuery(id+"F6.wireOp",EDGE,"E40"),sQuery(id+"F6.wireOp",EDGE,"E41"),sQuery(id+"F6.wireOp",EDGE,"E42"),sQuery(id+"F6.wireOp",EDGE,"E43"),sQuery(id+"F6.wireOp",EDGE,"E44")])],"isStart":false}),makeQuery(id+"F9.opExtrude","SWEPT_FACE",FACE,{"disambiguationData":[OSD([sQuery(id+"F8.wireOp",EDGE,"E45")])]})]});
            var Q7;
            Q7=makeQuery(id+"F10.opPattern","COPY",EDGE,{"derivedFrom":makeQuery(id+"F9.boolean.opBoolean","INTERSECT",EDGE,{"derivedFrom":[makeQuery(id+"F7.opExtrude","CAP_FACE",FACE,{"disambiguationData":[OSD([sQuery(id+"F6.wireOp",EDGE,"E20"),sQuery(id+"F6.wireOp",EDGE,"E21"),sQuery(id+"F6.wireOp",EDGE,"E22"),sQuery(id+"F6.wireOp",EDGE,"E23"),sQuery(id+"F6.wireOp",EDGE,"E24"),sQuery(id+"F6.wireOp",EDGE,"E25"),sQuery(id+"F6.wireOp",EDGE,"E26"),sQuery(id+"F6.wireOp",EDGE,"E27"),sQuery(id+"F6.wireOp",EDGE,"E28"),sQuery(id+"F6.wireOp",EDGE,"E29"),sQuery(id+"F6.wireOp",EDGE,"E30"),sQuery(id+"F6.wireOp",EDGE,"E31"),sQuery(id+"F6.wireOp",EDGE,"E32"),sQuery(id+"F6.wireOp",EDGE,"E33"),sQuery(id+"F6.wireOp",EDGE,"E34"),sQuery(id+"F6.wireOp",EDGE,"E35"),sQuery(id+"F6.wireOp",EDGE,"E36"),sQuery(id+"F6.wireOp",EDGE,"E37"),sQuery(id+"F6.wireOp",EDGE,"E38"),sQuery(id+"F6.wireOp",EDGE,"E39"),sQuery(id+"F6.wireOp",EDGE,"E40"),sQuery(id+"F6.wireOp",EDGE,"E41"),sQuery(id+"F6.wireOp",EDGE,"E42"),sQuery(id+"F6.wireOp",EDGE,"E43"),sQuery(id+"F6.wireOp",EDGE,"E44")])],"isStart":true}),makeQuery(id+"F9.opExtrude","SWEPT_FACE",FACE,{"disambiguationData":[OSD([sQuery(id+"F8.wireOp",EDGE,"E45")])]})]}),"instanceName":"7"});
            var Q8;
            Q8=makeQuery(id+"F10.opPattern","COPY",EDGE,{"derivedFrom":makeQuery(id+"F9.boolean.opBoolean","INTERSECT",EDGE,{"derivedFrom":[makeQuery(id+"F7.opExtrude","CAP_FACE",FACE,{"disambiguationData":[OSD([sQuery(id+"F6.wireOp",EDGE,"E20"),sQuery(id+"F6.wireOp",EDGE,"E21"),sQuery(id+"F6.wireOp",EDGE,"E22"),sQuery(id+"F6.wireOp",EDGE,"E23"),sQuery(id+"F6.wireOp",EDGE,"E24"),sQuery(id+"F6.wireOp",EDGE,"E25"),sQuery(id+"F6.wireOp",EDGE,"E26"),sQuery(id+"F6.wireOp",EDGE,"E27"),sQuery(id+"F6.wireOp",EDGE,"E28"),sQuery(id+"F6.wireOp",EDGE,"E29"),sQuery(id+"F6.wireOp",EDGE,"E30"),sQuery(id+"F6.wireOp",EDGE,"E31"),sQuery(id+"F6.wireOp",EDGE,"E32"),sQuery(id+"F6.wireOp",EDGE,"E33"),sQuery(id+"F6.wireOp",EDGE,"E34"),sQuery(id+"F6.wireOp",EDGE,"E35"),sQuery(id+"F6.wireOp",EDGE,"E36"),sQuery(id+"F6.wireOp",EDGE,"E37"),sQuery(id+"F6.wireOp",EDGE,"E38"),sQuery(id+"F6.wireOp",EDGE,"E39"),sQuery(id+"F6.wireOp",EDGE,"E40"),sQuery(id+"F6.wireOp",EDGE,"E41"),sQuery(id+"F6.wireOp",EDGE,"E42"),sQuery(id+"F6.wireOp",EDGE,"E43"),sQuery(id+"F6.wireOp",EDGE,"E44")])],"isStart":false}),makeQuery(id+"F9.opExtrude","SWEPT_FACE",FACE,{"disambiguationData":[OSD([sQuery(id+"F8.wireOp",EDGE,"E45")])]})]}),"instanceName":"7"});
            var Q9;
            Q9=makeQuery(id+"F10.opPattern","COPY",EDGE,{"derivedFrom":makeQuery(id+"F9.boolean.opBoolean","INTERSECT",EDGE,{"derivedFrom":[makeQuery(id+"F7.opExtrude","CAP_FACE",FACE,{"disambiguationData":[OSD([sQuery(id+"F6.wireOp",EDGE,"E20"),sQuery(id+"F6.wireOp",EDGE,"E21"),sQuery(id+"F6.wireOp",EDGE,"E22"),sQuery(id+"F6.wireOp",EDGE,"E23"),sQuery(id+"F6.wireOp",EDGE,"E24"),sQuery(id+"F6.wireOp",EDGE,"E25"),sQuery(id+"F6.wireOp",EDGE,"E26"),sQuery(id+"F6.wireOp",EDGE,"E27"),sQuery(id+"F6.wireOp",EDGE,"E28"),sQuery(id+"F6.wireOp",EDGE,"E29"),sQuery(id+"F6.wireOp",EDGE,"E30"),sQuery(id+"F6.wireOp",EDGE,"E31"),sQuery(id+"F6.wireOp",EDGE,"E32"),sQuery(id+"F6.wireOp",EDGE,"E33"),sQuery(id+"F6.wireOp",EDGE,"E34"),sQuery(id+"F6.wireOp",EDGE,"E35"),sQuery(id+"F6.wireOp",EDGE,"E36"),sQuery(id+"F6.wireOp",EDGE,"E37"),sQuery(id+"F6.wireOp",EDGE,"E38"),sQuery(id+"F6.wireOp",EDGE,"E39"),sQuery(id+"F6.wireOp",EDGE,"E40"),sQuery(id+"F6.wireOp",EDGE,"E41"),sQuery(id+"F6.wireOp",EDGE,"E42"),sQuery(id+"F6.wireOp",EDGE,"E43"),sQuery(id+"F6.wireOp",EDGE,"E44")])],"isStart":true}),makeQuery(id+"F9.opExtrude","SWEPT_FACE",FACE,{"disambiguationData":[OSD([sQuery(id+"F8.wireOp",EDGE,"E45")])]})]}),"instanceName":"6"});
            var Q10;
            Q10=makeQuery(id+"F10.opPattern","COPY",EDGE,{"derivedFrom":makeQuery(id+"F9.boolean.opBoolean","INTERSECT",EDGE,{"derivedFrom":[makeQuery(id+"F7.opExtrude","CAP_FACE",FACE,{"disambiguationData":[OSD([sQuery(id+"F6.wireOp",EDGE,"E20"),sQuery(id+"F6.wireOp",EDGE,"E21"),sQuery(id+"F6.wireOp",EDGE,"E22"),sQuery(id+"F6.wireOp",EDGE,"E23"),sQuery(id+"F6.wireOp",EDGE,"E24"),sQuery(id+"F6.wireOp",EDGE,"E25"),sQuery(id+"F6.wireOp",EDGE,"E26"),sQuery(id+"F6.wireOp",EDGE,"E27"),sQuery(id+"F6.wireOp",EDGE,"E28"),sQuery(id+"F6.wireOp",EDGE,"E29"),sQuery(id+"F6.wireOp",EDGE,"E30"),sQuery(id+"F6.wireOp",EDGE,"E31"),sQuery(id+"F6.wireOp",EDGE,"E32"),sQuery(id+"F6.wireOp",EDGE,"E33"),sQuery(id+"F6.wireOp",EDGE,"E34"),sQuery(id+"F6.wireOp",EDGE,"E35"),sQuery(id+"F6.wireOp",EDGE,"E36"),sQuery(id+"F6.wireOp",EDGE,"E37"),sQuery(id+"F6.wireOp",EDGE,"E38"),sQuery(id+"F6.wireOp",EDGE,"E39"),sQuery(id+"F6.wireOp",EDGE,"E40"),sQuery(id+"F6.wireOp",EDGE,"E41"),sQuery(id+"F6.wireOp",EDGE,"E42"),sQuery(id+"F6.wireOp",EDGE,"E43"),sQuery(id+"F6.wireOp",EDGE,"E44")])],"isStart":false}),makeQuery(id+"F9.opExtrude","SWEPT_FACE",FACE,{"disambiguationData":[OSD([sQuery(id+"F8.wireOp",EDGE,"E45")])]})]}),"instanceName":"6"});
            var Q11;
            Q11=makeQuery(id+"F10.opPattern","COPY",EDGE,{"derivedFrom":makeQuery(id+"F9.boolean.opBoolean","INTERSECT",EDGE,{"derivedFrom":[makeQuery(id+"F7.opExtrude","CAP_FACE",FACE,{"disambiguationData":[OSD([sQuery(id+"F6.wireOp",EDGE,"E20"),sQuery(id+"F6.wireOp",EDGE,"E21"),sQuery(id+"F6.wireOp",EDGE,"E22"),sQuery(id+"F6.wireOp",EDGE,"E23"),sQuery(id+"F6.wireOp",EDGE,"E24"),sQuery(id+"F6.wireOp",EDGE,"E25"),sQuery(id+"F6.wireOp",EDGE,"E26"),sQuery(id+"F6.wireOp",EDGE,"E27"),sQuery(id+"F6.wireOp",EDGE,"E28"),sQuery(id+"F6.wireOp",EDGE,"E29"),sQuery(id+"F6.wireOp",EDGE,"E30"),sQuery(id+"F6.wireOp",EDGE,"E31"),sQuery(id+"F6.wireOp",EDGE,"E32"),sQuery(id+"F6.wireOp",EDGE,"E33"),sQuery(id+"F6.wireOp",EDGE,"E34"),sQuery(id+"F6.wireOp",EDGE,"E35"),sQuery(id+"F6.wireOp",EDGE,"E36"),sQuery(id+"F6.wireOp",EDGE,"E37"),sQuery(id+"F6.wireOp",EDGE,"E38"),sQuery(id+"F6.wireOp",EDGE,"E39"),sQuery(id+"F6.wireOp",EDGE,"E40"),sQuery(id+"F6.wireOp",EDGE,"E41"),sQuery(id+"F6.wireOp",EDGE,"E42"),sQuery(id+"F6.wireOp",EDGE,"E43"),sQuery(id+"F6.wireOp",EDGE,"E44")])],"isStart":true}),makeQuery(id+"F9.opExtrude","SWEPT_FACE",FACE,{"disambiguationData":[OSD([sQuery(id+"F8.wireOp",EDGE,"E45")])]})]}),"instanceName":"5"});
            var Q12;
            Q12=makeQuery(id+"F10.opPattern","COPY",EDGE,{"derivedFrom":makeQuery(id+"F9.boolean.opBoolean","INTERSECT",EDGE,{"derivedFrom":[makeQuery(id+"F7.opExtrude","CAP_FACE",FACE,{"disambiguationData":[OSD([sQuery(id+"F6.wireOp",EDGE,"E20"),sQuery(id+"F6.wireOp",EDGE,"E21"),sQuery(id+"F6.wireOp",EDGE,"E22"),sQuery(id+"F6.wireOp",EDGE,"E23"),sQuery(id+"F6.wireOp",EDGE,"E24"),sQuery(id+"F6.wireOp",EDGE,"E25"),sQuery(id+"F6.wireOp",EDGE,"E26"),sQuery(id+"F6.wireOp",EDGE,"E27"),sQuery(id+"F6.wireOp",EDGE,"E28"),sQuery(id+"F6.wireOp",EDGE,"E29"),sQuery(id+"F6.wireOp",EDGE,"E30"),sQuery(id+"F6.wireOp",EDGE,"E31"),sQuery(id+"F6.wireOp",EDGE,"E32"),sQuery(id+"F6.wireOp",EDGE,"E33"),sQuery(id+"F6.wireOp",EDGE,"E34"),sQuery(id+"F6.wireOp",EDGE,"E35"),sQuery(id+"F6.wireOp",EDGE,"E36"),sQuery(id+"F6.wireOp",EDGE,"E37"),sQuery(id+"F6.wireOp",EDGE,"E38"),sQuery(id+"F6.wireOp",EDGE,"E39"),sQuery(id+"F6.wireOp",EDGE,"E40"),sQuery(id+"F6.wireOp",EDGE,"E41"),sQuery(id+"F6.wireOp",EDGE,"E42"),sQuery(id+"F6.wireOp",EDGE,"E43"),sQuery(id+"F6.wireOp",EDGE,"E44")])],"isStart":false}),makeQuery(id+"F9.opExtrude","SWEPT_FACE",FACE,{"disambiguationData":[OSD([sQuery(id+"F8.wireOp",EDGE,"E45")])]})]}),"instanceName":"4"});
            var Q13;
            Q13=makeQuery(id+"F10.opPattern","COPY",EDGE,{"derivedFrom":makeQuery(id+"F9.boolean.opBoolean","INTERSECT",EDGE,{"derivedFrom":[makeQuery(id+"F7.opExtrude","CAP_FACE",FACE,{"disambiguationData":[OSD([sQuery(id+"F6.wireOp",EDGE,"E20"),sQuery(id+"F6.wireOp",EDGE,"E21"),sQuery(id+"F6.wireOp",EDGE,"E22"),sQuery(id+"F6.wireOp",EDGE,"E23"),sQuery(id+"F6.wireOp",EDGE,"E24"),sQuery(id+"F6.wireOp",EDGE,"E25"),sQuery(id+"F6.wireOp",EDGE,"E26"),sQuery(id+"F6.wireOp",EDGE,"E27"),sQuery(id+"F6.wireOp",EDGE,"E28"),sQuery(id+"F6.wireOp",EDGE,"E29"),sQuery(id+"F6.wireOp",EDGE,"E30"),sQuery(id+"F6.wireOp",EDGE,"E31"),sQuery(id+"F6.wireOp",EDGE,"E32"),sQuery(id+"F6.wireOp",EDGE,"E33"),sQuery(id+"F6.wireOp",EDGE,"E34"),sQuery(id+"F6.wireOp",EDGE,"E35"),sQuery(id+"F6.wireOp",EDGE,"E36"),sQuery(id+"F6.wireOp",EDGE,"E37"),sQuery(id+"F6.wireOp",EDGE,"E38"),sQuery(id+"F6.wireOp",EDGE,"E39"),sQuery(id+"F6.wireOp",EDGE,"E40"),sQuery(id+"F6.wireOp",EDGE,"E41"),sQuery(id+"F6.wireOp",EDGE,"E42"),sQuery(id+"F6.wireOp",EDGE,"E43"),sQuery(id+"F6.wireOp",EDGE,"E44")])],"isStart":true}),makeQuery(id+"F9.opExtrude","SWEPT_FACE",FACE,{"disambiguationData":[OSD([sQuery(id+"F8.wireOp",EDGE,"E45")])]})]}),"instanceName":"3"});
            var Q14;
            Q14=makeQuery(id+"F10.opPattern","COPY",EDGE,{"derivedFrom":makeQuery(id+"F9.boolean.opBoolean","INTERSECT",EDGE,{"derivedFrom":[makeQuery(id+"F7.opExtrude","CAP_FACE",FACE,{"disambiguationData":[OSD([sQuery(id+"F6.wireOp",EDGE,"E20"),sQuery(id+"F6.wireOp",EDGE,"E21"),sQuery(id+"F6.wireOp",EDGE,"E22"),sQuery(id+"F6.wireOp",EDGE,"E23"),sQuery(id+"F6.wireOp",EDGE,"E24"),sQuery(id+"F6.wireOp",EDGE,"E25"),sQuery(id+"F6.wireOp",EDGE,"E26"),sQuery(id+"F6.wireOp",EDGE,"E27"),sQuery(id+"F6.wireOp",EDGE,"E28"),sQuery(id+"F6.wireOp",EDGE,"E29"),sQuery(id+"F6.wireOp",EDGE,"E30"),sQuery(id+"F6.wireOp",EDGE,"E31"),sQuery(id+"F6.wireOp",EDGE,"E32"),sQuery(id+"F6.wireOp",EDGE,"E33"),sQuery(id+"F6.wireOp",EDGE,"E34"),sQuery(id+"F6.wireOp",EDGE,"E35"),sQuery(id+"F6.wireOp",EDGE,"E36"),sQuery(id+"F6.wireOp",EDGE,"E37"),sQuery(id+"F6.wireOp",EDGE,"E38"),sQuery(id+"F6.wireOp",EDGE,"E39"),sQuery(id+"F6.wireOp",EDGE,"E40"),sQuery(id+"F6.wireOp",EDGE,"E41"),sQuery(id+"F6.wireOp",EDGE,"E42"),sQuery(id+"F6.wireOp",EDGE,"E43"),sQuery(id+"F6.wireOp",EDGE,"E44")])],"isStart":false}),makeQuery(id+"F9.opExtrude","SWEPT_FACE",FACE,{"disambiguationData":[OSD([sQuery(id+"F8.wireOp",EDGE,"E45")])]})]}),"instanceName":"5"});
            var Q15;
            Q15=makeQuery(id+"F10.opPattern","COPY",EDGE,{"derivedFrom":makeQuery(id+"F9.boolean.opBoolean","INTERSECT",EDGE,{"derivedFrom":[makeQuery(id+"F7.opExtrude","CAP_FACE",FACE,{"disambiguationData":[OSD([sQuery(id+"F6.wireOp",EDGE,"E20"),sQuery(id+"F6.wireOp",EDGE,"E21"),sQuery(id+"F6.wireOp",EDGE,"E22"),sQuery(id+"F6.wireOp",EDGE,"E23"),sQuery(id+"F6.wireOp",EDGE,"E24"),sQuery(id+"F6.wireOp",EDGE,"E25"),sQuery(id+"F6.wireOp",EDGE,"E26"),sQuery(id+"F6.wireOp",EDGE,"E27"),sQuery(id+"F6.wireOp",EDGE,"E28"),sQuery(id+"F6.wireOp",EDGE,"E29"),sQuery(id+"F6.wireOp",EDGE,"E30"),sQuery(id+"F6.wireOp",EDGE,"E31"),sQuery(id+"F6.wireOp",EDGE,"E32"),sQuery(id+"F6.wireOp",EDGE,"E33"),sQuery(id+"F6.wireOp",EDGE,"E34"),sQuery(id+"F6.wireOp",EDGE,"E35"),sQuery(id+"F6.wireOp",EDGE,"E36"),sQuery(id+"F6.wireOp",EDGE,"E37"),sQuery(id+"F6.wireOp",EDGE,"E38"),sQuery(id+"F6.wireOp",EDGE,"E39"),sQuery(id+"F6.wireOp",EDGE,"E40"),sQuery(id+"F6.wireOp",EDGE,"E41"),sQuery(id+"F6.wireOp",EDGE,"E42"),sQuery(id+"F6.wireOp",EDGE,"E43"),sQuery(id+"F6.wireOp",EDGE,"E44")])],"isStart":true}),makeQuery(id+"F9.opExtrude","SWEPT_FACE",FACE,{"disambiguationData":[OSD([sQuery(id+"F8.wireOp",EDGE,"E45")])]})]}),"instanceName":"4"});
            fillet(context, id + "F17", {"entities" : qUnion([Q0, Q1, Q2, Q3, Q4, Q5, Q6, Q7, Q8, Q9, Q10, Q11, Q12, Q13, Q14, Q15]), "radius" : 5 * mm, "tangentPropagation" : true, "allowEdgeOverflow" : false});
        }
        {
            var Q0;
            Q0=makeQuery(id+"F13.opPattern","COPY",EDGE,{"derivedFrom":makeQuery(id+"F12.opExtrude","SWEPT_EDGE",EDGE,{"disambiguationData":[OSD([sQuery(id+"F11.wireOp",EDGE,"E51.7"),sQuery(id+"F11.wireOp",EDGE,"E54.trimOffspring")])]}),"instanceName":"3"});
            fillet(context, id + "F18", {"entities" : qUnion([Q0]), "radius" : 5 * mm, "tangentPropagation" : true, "allowEdgeOverflow" : false});
        }
        {
            var Q0;
            Q0=makeQuery(id+"F13.opPattern","COPY",EDGE,{"derivedFrom":makeQuery(id+"F12.opExtrude","CAP_EDGE",EDGE,{"disambiguationData":[OSD([sQuery(id+"F11.wireOp",EDGE,"E56.trimOffspring")])],"isStart":true}),"instanceName":"3"});
            var Q1;
            Q1=makeQuery(id+"F13.opPattern","COPY",EDGE,{"derivedFrom":makeQuery(id+"F12.opExtrude","SWEPT_EDGE",EDGE,{"disambiguationData":[OSD([sQuery(id+"F11.wireOp",EDGE,"E56.trimOffspring"),sQuery(id+"F11.wireOp",EDGE,"E57.trimOffspring")])]}),"instanceName":"3"});
            fillet(context, id + "F19", {"entities" : qUnion([Q0, Q1]), "radius" : 5 * mm, "tangentPropagation" : true, "allowEdgeOverflow" : false});
        }
        {
            var Q0;
            Q0=makeQuery(id+"F13.opPattern","COPY",EDGE,{"derivedFrom":makeQuery(id+"F12.opExtrude","CAP_EDGE",EDGE,{"disambiguationData":[OSD([sQuery(id+"F11.wireOp",EDGE,"E56.trimOffspring")])],"isStart":true}),"instanceName":"2"});
            var Q1;
            Q1=makeQuery(id+"F13.opPattern","COPY",EDGE,{"derivedFrom":makeQuery(id+"F12.opExtrude","SWEPT_EDGE",EDGE,{"disambiguationData":[OSD([sQuery(id+"F11.wireOp",EDGE,"E56.trimOffspring"),sQuery(id+"F11.wireOp",EDGE,"E57.trimOffspring")])]}),"instanceName":"2"});
            fillet(context, id + "F20", {"entities" : qUnion([Q0, Q1]), "radius" : 5 * mm, "tangentPropagation" : true, "allowEdgeOverflow" : false});
        }
        {
            var Q0;
            Q0=makeQuery(id+"F13.opPattern","COPY",EDGE,{"derivedFrom":makeQuery(id+"F12.opExtrude","CAP_EDGE",EDGE,{"disambiguationData":[OSD([sQuery(id+"F11.wireOp",EDGE,"E51.7")])],"isStart":true}),"instanceName":"2"});
            var Q1;
            Q1=makeQuery(id+"F13.opPattern","COPY",EDGE,{"derivedFrom":makeQuery(id+"F12.opExtrude","SWEPT_EDGE",EDGE,{"disambiguationData":[OSD([sQuery(id+"F11.wireOp",EDGE,"E51.7"),sQuery(id+"F11.wireOp",EDGE,"E54.trimOffspring")])]}),"instanceName":"2"});
            fillet(context, id + "F21", {"entities" : qUnion([Q0, Q1]), "radius" : 5 * mm, "tangentPropagation" : true, "allowEdgeOverflow" : false});
        }
        {
            var Q0;
            Q0=makeQuery(id+"F13.opPattern","COPY",EDGE,{"derivedFrom":makeQuery(id+"F12.opExtrude","CAP_EDGE",EDGE,{"disambiguationData":[OSD([sQuery(id+"F11.wireOp",EDGE,"E56.trimOffspring")])],"isStart":true}),"instanceName":"1"});
            fillet(context, id + "F22", {"entities" : qUnion([Q0]), "radius" : 5 * mm, "tangentPropagation" : true, "allowEdgeOverflow" : false});
        }
        {
            var Q0;
            Q0=makeQuery(id+"F13.opPattern","COPY",EDGE,{"derivedFrom":makeQuery(id+"F12.opExtrude","CAP_EDGE",EDGE,{"disambiguationData":[OSD([sQuery(id+"F11.wireOp",EDGE,"E51.7")])],"isStart":true}),"instanceName":"1"});
            fillet(context, id + "F23", {"entities" : qUnion([Q0]), "radius" : 5 * mm, "tangentPropagation" : true, "allowEdgeOverflow" : false});
        }
        {
            var Q0;
            Q0=makeQuery(id+"F12.opExtrude","CAP_EDGE",EDGE,{"disambiguationData":[OSD([sQuery(id+"F11.wireOp",EDGE,"E56.trimOffspring")])],"isStart":true});
            var Q1;
            Q1=makeQuery(id+"F12.opExtrude","SWEPT_EDGE",EDGE,{"disambiguationData":[OSD([sQuery(id+"F11.wireOp",EDGE,"E56.trimOffspring"),sQuery(id+"F11.wireOp",EDGE,"E57.trimOffspring")])]});
            fillet(context, id + "F24", {"entities" : qUnion([Q0, Q1]), "radius" : 5 * mm, "tangentPropagation" : true, "allowEdgeOverflow" : false});
        }
        {
            var Q0;
            Q0=makeQuery(id+"F12.opExtrude","CAP_EDGE",EDGE,{"disambiguationData":[OSD([sQuery(id+"F11.wireOp",EDGE,"E51.7")])],"isStart":true});
            fillet(context, id + "F25", {"entities" : qUnion([Q0]), "radius" : 5 * mm, "tangentPropagation" : true, "allowEdgeOverflow" : false});
        }
    });
